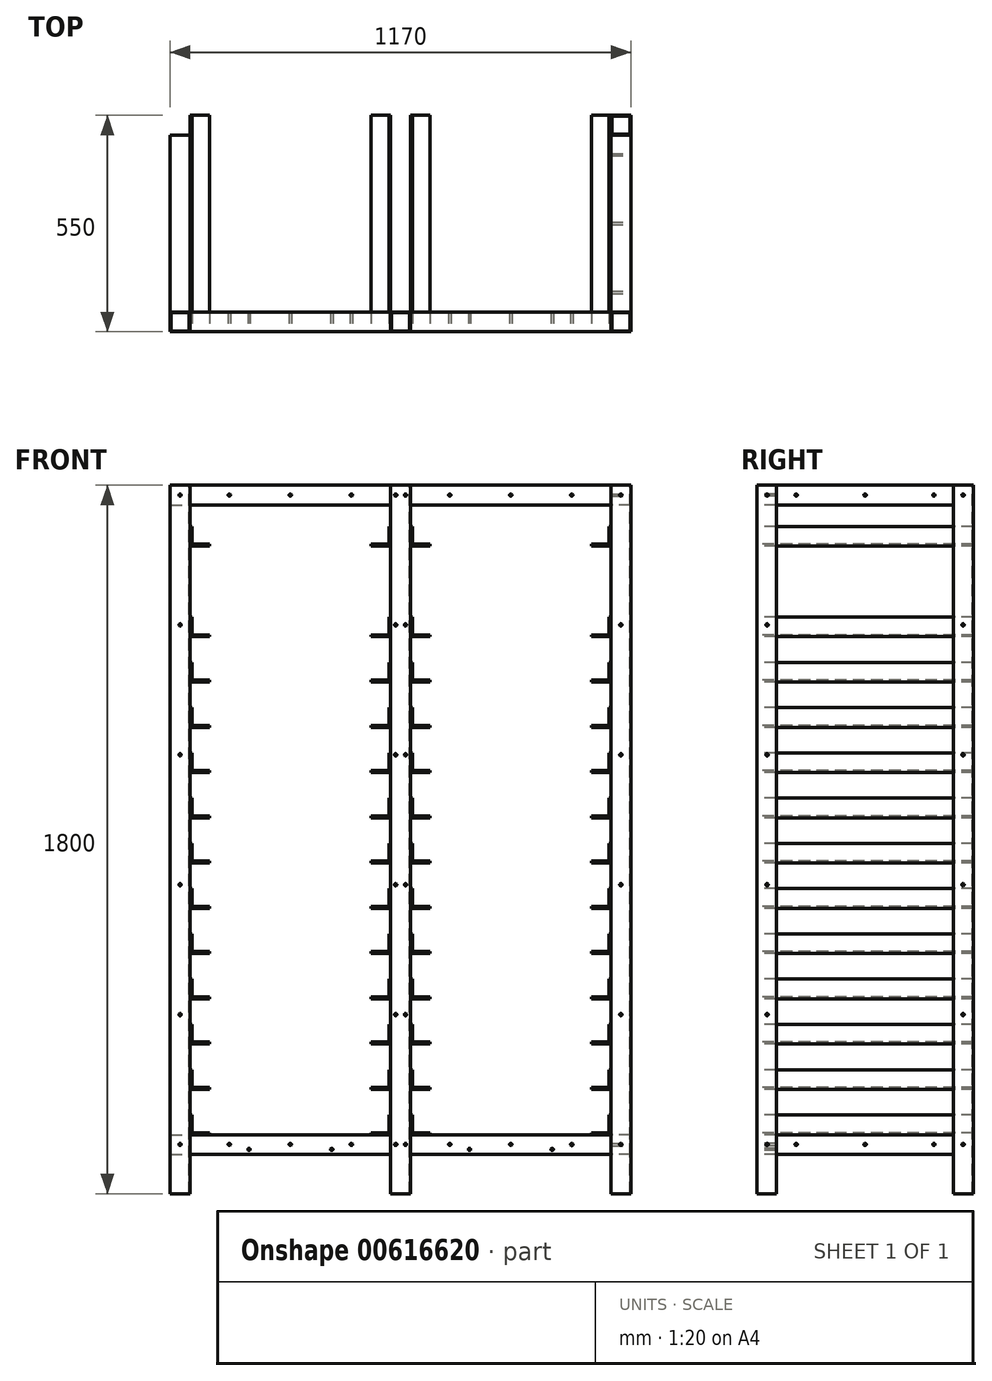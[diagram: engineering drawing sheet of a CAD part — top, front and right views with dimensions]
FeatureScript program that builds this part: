
annotation { "Feature Type Name" : "Feature", "Feature Type Description" : "" }
export const myFeature = defineFeature(function(context is Context, id is Id, definition is map)
    precondition{}
    {
        {
            var Q0;
            Q0=qCreatedBy(makeId("Front.planeOp"),FACE);
            var sketch = newSketch(context, id + "F0", { "sketchPlane" : qUnion([Q0])});
            skLineSegment(sketch, "E0.bottom", {"start": v(-1040.9, 69.44) * mm, "end": v(-990.9, 69.44) * mm});
            skLineSegment(sketch, "E0.top", {"start": v(-1040.9, 1869.44) * mm, "end": v(-990.9, 1869.44) * mm});
            skLineSegment(sketch, "E0.left", {"start": v(-1040.9, 69.44) * mm, "end": v(-1040.9, 1869.44) * mm});
            skLineSegment(sketch, "E0.right", {"start": v(-990.9, 69.44) * mm, "end": v(-990.9, 1869.44) * mm});
            skLineSegment(sketch, "E1.bottom", {"start": v(-990.9, 219.44) * mm, "end": v(-480.9, 219.44) * mm});
            skLineSegment(sketch, "E1.top", {"start": v(-990.9, 169.44) * mm, "end": v(-480.9, 169.44) * mm});
            skLineSegment(sketch, "E1.left", {"start": v(-990.9, 219.44) * mm, "end": v(-990.9, 169.44) * mm});
            skLineSegment(sketch, "E1.right", {"start": v(-480.9, 219.44) * mm, "end": v(-480.9, 169.44) * mm});
            skLineSegment(sketch, "E2.bottom", {"start": v(-980.9, 320.94) * mm, "end": v(-490.9, 320.94) * mm});
            skLineSegment(sketch, "E2.top", {"start": v(-980.9, 224.94) * mm, "end": v(-490.9, 224.94) * mm});
            skLineSegment(sketch, "E2.left", {"start": v(-980.9, 320.94) * mm, "end": v(-980.9, 224.94) * mm});
            skLineSegment(sketch, "E2.right", {"start": v(-490.9, 320.94) * mm, "end": v(-490.9, 224.94) * mm});
            skPoint(sketch, "E3", {"position": v(-990.9, 194.44) * mm});
            skLineSegment(sketch, "E4", {"start": v(-985.9, 269.44) * mm, "end": v(-985.9, 224.44) * mm});
            skLineSegment(sketch, "E5", {"start": v(-985.9, 224.44) * mm, "end": v(-940.9, 224.44) * mm});
            skLineSegment(sketch, "E6", {"start": v(-985.9, 269.44) * mm, "end": v(-990.9, 269.44) * mm});
            skLineSegment(sketch, "E7", {"start": v(-990.9, 269.44) * mm, "end": v(-990.9, 219.44) * mm});
            skLineSegment(sketch, "E8", {"start": v(-990.9, 219.44) * mm, "end": v(-940.9, 219.44) * mm});
            skLineSegment(sketch, "E9", {"start": v(-940.9, 219.44) * mm, "end": v(-940.9, 224.44) * mm});
            skLineSegment(sketch, "E10.0.1.0", {"start": v(-990.9, 384.44) * mm, "end": v(-990.9, 334.44) * mm});
            skLineSegment(sketch, "E10.0.1.1", {"start": v(-985.9, 339.44) * mm, "end": v(-940.9, 339.44) * mm});
            skLineSegment(sketch, "E10.0.1.2", {"start": v(-990.9, 334.44) * mm, "end": v(-940.9, 334.44) * mm});
            skLineSegment(sketch, "E10.0.1.3", {"start": v(-985.9, 384.44) * mm, "end": v(-985.9, 339.44) * mm});
            skLineSegment(sketch, "E10.0.1.4", {"start": v(-940.9, 334.44) * mm, "end": v(-940.9, 339.44) * mm});
            skLineSegment(sketch, "E10.0.1.5", {"start": v(-985.9, 384.44) * mm, "end": v(-990.9, 384.44) * mm});
            skLineSegment(sketch, "E10.0.2.0", {"start": v(-990.9, 499.44) * mm, "end": v(-990.9, 449.44) * mm});
            skLineSegment(sketch, "E10.0.2.1", {"start": v(-985.9, 454.44) * mm, "end": v(-940.9, 454.44) * mm});
            skLineSegment(sketch, "E10.0.2.2", {"start": v(-990.9, 449.44) * mm, "end": v(-940.9, 449.44) * mm});
            skLineSegment(sketch, "E10.0.2.3", {"start": v(-985.9, 499.44) * mm, "end": v(-985.9, 454.44) * mm});
            skLineSegment(sketch, "E10.0.2.4", {"start": v(-940.9, 449.44) * mm, "end": v(-940.9, 454.44) * mm});
            skLineSegment(sketch, "E10.0.2.5", {"start": v(-985.9, 499.44) * mm, "end": v(-990.9, 499.44) * mm});
            skLineSegment(sketch, "E10.0.3.0", {"start": v(-990.9, 614.44) * mm, "end": v(-990.9, 564.44) * mm});
            skLineSegment(sketch, "E10.0.3.1", {"start": v(-985.9, 569.44) * mm, "end": v(-940.9, 569.44) * mm});
            skLineSegment(sketch, "E10.0.3.2", {"start": v(-990.9, 564.44) * mm, "end": v(-940.9, 564.44) * mm});
            skLineSegment(sketch, "E10.0.3.3", {"start": v(-985.9, 614.44) * mm, "end": v(-985.9, 569.44) * mm});
            skLineSegment(sketch, "E10.0.3.4", {"start": v(-940.9, 564.44) * mm, "end": v(-940.9, 569.44) * mm});
            skLineSegment(sketch, "E10.0.3.5", {"start": v(-985.9, 614.44) * mm, "end": v(-990.9, 614.44) * mm});
            skLineSegment(sketch, "E10.0.4.0", {"start": v(-990.9, 729.44) * mm, "end": v(-990.9, 679.44) * mm});
            skLineSegment(sketch, "E10.0.4.1", {"start": v(-985.9, 684.44) * mm, "end": v(-940.9, 684.44) * mm});
            skLineSegment(sketch, "E10.0.4.2", {"start": v(-990.9, 679.44) * mm, "end": v(-940.9, 679.44) * mm});
            skLineSegment(sketch, "E10.0.4.3", {"start": v(-985.9, 729.44) * mm, "end": v(-985.9, 684.44) * mm});
            skLineSegment(sketch, "E10.0.4.4", {"start": v(-940.9, 679.44) * mm, "end": v(-940.9, 684.44) * mm});
            skLineSegment(sketch, "E10.0.4.5", {"start": v(-985.9, 729.44) * mm, "end": v(-990.9, 729.44) * mm});
            skLineSegment(sketch, "E10.0.5.0", {"start": v(-990.9, 844.44) * mm, "end": v(-990.9, 794.44) * mm});
            skLineSegment(sketch, "E10.0.5.1", {"start": v(-985.9, 799.44) * mm, "end": v(-940.9, 799.44) * mm});
            skLineSegment(sketch, "E10.0.5.2", {"start": v(-990.9, 794.44) * mm, "end": v(-940.9, 794.44) * mm});
            skLineSegment(sketch, "E10.0.5.3", {"start": v(-985.9, 844.44) * mm, "end": v(-985.9, 799.44) * mm});
            skLineSegment(sketch, "E10.0.5.4", {"start": v(-940.9, 794.44) * mm, "end": v(-940.9, 799.44) * mm});
            skLineSegment(sketch, "E10.0.5.5", {"start": v(-985.9, 844.44) * mm, "end": v(-990.9, 844.44) * mm});
            skLineSegment(sketch, "E10.0.6.0", {"start": v(-990.9, 959.44) * mm, "end": v(-990.9, 909.44) * mm});
            skLineSegment(sketch, "E10.0.6.1", {"start": v(-985.9, 914.44) * mm, "end": v(-940.9, 914.44) * mm});
            skLineSegment(sketch, "E10.0.6.2", {"start": v(-990.9, 909.44) * mm, "end": v(-940.9, 909.44) * mm});
            skLineSegment(sketch, "E10.0.6.3", {"start": v(-985.9, 959.44) * mm, "end": v(-985.9, 914.44) * mm});
            skLineSegment(sketch, "E10.0.6.4", {"start": v(-940.9, 909.44) * mm, "end": v(-940.9, 914.44) * mm});
            skLineSegment(sketch, "E10.0.6.5", {"start": v(-985.9, 959.44) * mm, "end": v(-990.9, 959.44) * mm});
            skLineSegment(sketch, "E10.0.7.0", {"start": v(-990.9, 1074.44) * mm, "end": v(-990.9, 1024.44) * mm});
            skLineSegment(sketch, "E10.0.7.1", {"start": v(-985.9, 1029.44) * mm, "end": v(-940.9, 1029.44) * mm});
            skLineSegment(sketch, "E10.0.7.2", {"start": v(-990.9, 1024.44) * mm, "end": v(-940.9, 1024.44) * mm});
            skLineSegment(sketch, "E10.0.7.3", {"start": v(-985.9, 1074.44) * mm, "end": v(-985.9, 1029.44) * mm});
            skLineSegment(sketch, "E10.0.7.4", {"start": v(-940.9, 1024.44) * mm, "end": v(-940.9, 1029.44) * mm});
            skLineSegment(sketch, "E10.0.7.5", {"start": v(-985.9, 1074.44) * mm, "end": v(-990.9, 1074.44) * mm});
            skLineSegment(sketch, "E10.0.8.0", {"start": v(-990.9, 1189.44) * mm, "end": v(-990.9, 1139.44) * mm});
            skLineSegment(sketch, "E10.0.8.1", {"start": v(-985.9, 1144.44) * mm, "end": v(-940.9, 1144.44) * mm});
            skLineSegment(sketch, "E10.0.8.2", {"start": v(-990.9, 1139.44) * mm, "end": v(-940.9, 1139.44) * mm});
            skLineSegment(sketch, "E10.0.8.3", {"start": v(-985.9, 1189.44) * mm, "end": v(-985.9, 1144.44) * mm});
            skLineSegment(sketch, "E10.0.8.4", {"start": v(-940.9, 1139.44) * mm, "end": v(-940.9, 1144.44) * mm});
            skLineSegment(sketch, "E10.0.8.5", {"start": v(-985.9, 1189.44) * mm, "end": v(-990.9, 1189.44) * mm});
            skLineSegment(sketch, "E10.0.9.0", {"start": v(-990.9, 1304.44) * mm, "end": v(-990.9, 1254.44) * mm});
            skLineSegment(sketch, "E10.0.9.1", {"start": v(-985.9, 1259.44) * mm, "end": v(-940.9, 1259.44) * mm});
            skLineSegment(sketch, "E10.0.9.2", {"start": v(-990.9, 1254.44) * mm, "end": v(-940.9, 1254.44) * mm});
            skLineSegment(sketch, "E10.0.9.3", {"start": v(-985.9, 1304.44) * mm, "end": v(-985.9, 1259.44) * mm});
            skLineSegment(sketch, "E10.0.9.4", {"start": v(-940.9, 1254.44) * mm, "end": v(-940.9, 1259.44) * mm});
            skLineSegment(sketch, "E10.0.9.5", {"start": v(-985.9, 1304.44) * mm, "end": v(-990.9, 1304.44) * mm});
            skLineSegment(sketch, "E10.0.10.0", {"start": v(-990.9, 1419.44) * mm, "end": v(-990.9, 1369.44) * mm});
            skLineSegment(sketch, "E10.0.10.1", {"start": v(-985.9, 1374.44) * mm, "end": v(-940.9, 1374.44) * mm});
            skLineSegment(sketch, "E10.0.10.2", {"start": v(-990.9, 1369.44) * mm, "end": v(-940.9, 1369.44) * mm});
            skLineSegment(sketch, "E10.0.10.3", {"start": v(-985.9, 1419.44) * mm, "end": v(-985.9, 1374.44) * mm});
            skLineSegment(sketch, "E10.0.10.4", {"start": v(-940.9, 1369.44) * mm, "end": v(-940.9, 1374.44) * mm});
            skLineSegment(sketch, "E10.0.10.5", {"start": v(-985.9, 1419.44) * mm, "end": v(-990.9, 1419.44) * mm});
            skLineSegment(sketch, "E10.0.11.0", {"start": v(-990.9, 1534.44) * mm, "end": v(-990.9, 1484.44) * mm});
            skLineSegment(sketch, "E10.0.11.1", {"start": v(-985.9, 1489.44) * mm, "end": v(-940.9, 1489.44) * mm});
            skLineSegment(sketch, "E10.0.11.2", {"start": v(-990.9, 1484.44) * mm, "end": v(-940.9, 1484.44) * mm});
            skLineSegment(sketch, "E10.0.11.3", {"start": v(-985.9, 1534.44) * mm, "end": v(-985.9, 1489.44) * mm});
            skLineSegment(sketch, "E10.0.11.4", {"start": v(-940.9, 1484.44) * mm, "end": v(-940.9, 1489.44) * mm});
            skLineSegment(sketch, "E10.0.11.5", {"start": v(-985.9, 1534.44) * mm, "end": v(-990.9, 1534.44) * mm});
            skLineSegment(sketch, "E10.direction1", {"start": v(-990.9, 219.44) * mm, "end": v(-950, 219.44) * mm, "construction": true});
            skLineSegment(sketch, "E10.direction2", {"start": v(-990.9, 219.44) * mm, "end": v(-990.9, 334.44) * mm, "construction": true});
            skLineSegment(sketch, "E11", {"start": v(-735.9, 219.44) * mm, "end": v(-735.9, 1014.16) * mm, "construction": true});
            skLineSegment(sketch, "E12.MirrorCS", {"start": v(-530.9, 909.44) * mm, "end": v(-530.9, 914.44) * mm});
            skLineSegment(sketch, "E13.MirrorCS", {"start": v(-485.9, 1074.44) * mm, "end": v(-480.9, 1074.44) * mm});
            skLineSegment(sketch, "E14.MirrorCS", {"start": v(-530.9, 1024.44) * mm, "end": v(-530.9, 1029.44) * mm});
            skLineSegment(sketch, "E15.MirrorCS", {"start": v(-485.9, 1029.44) * mm, "end": v(-530.9, 1029.44) * mm});
            skLineSegment(sketch, "E16.MirrorCS", {"start": v(-485.9, 914.44) * mm, "end": v(-530.9, 914.44) * mm});
            skLineSegment(sketch, "E17.MirrorCS", {"start": v(-485.9, 1304.44) * mm, "end": v(-480.9, 1304.44) * mm});
            skLineSegment(sketch, "E18.MirrorCS", {"start": v(-480.9, 1074.44) * mm, "end": v(-480.9, 1024.44) * mm});
            skLineSegment(sketch, "E19.MirrorCS", {"start": v(-485.9, 1489.44) * mm, "end": v(-530.9, 1489.44) * mm});
            skLineSegment(sketch, "E20.MirrorCS", {"start": v(-485.9, 959.44) * mm, "end": v(-480.9, 959.44) * mm});
            skLineSegment(sketch, "E21.MirrorCS", {"start": v(-485.9, 1304.44) * mm, "end": v(-485.9, 1259.44) * mm});
            skLineSegment(sketch, "E22.MirrorCS", {"start": v(-530.9, 1369.44) * mm, "end": v(-530.9, 1374.44) * mm});
            skLineSegment(sketch, "E23.MirrorCS", {"start": v(-480.9, 1189.44) * mm, "end": v(-480.9, 1139.44) * mm});
            skLineSegment(sketch, "E24.MirrorCS", {"start": v(-485.9, 1144.44) * mm, "end": v(-530.9, 1144.44) * mm});
            skLineSegment(sketch, "E25.MirrorCS", {"start": v(-485.9, 1419.44) * mm, "end": v(-485.9, 1374.44) * mm});
            skLineSegment(sketch, "E26.MirrorCS", {"start": v(-485.9, 959.44) * mm, "end": v(-485.9, 914.44) * mm});
            skLineSegment(sketch, "E27.MirrorCS", {"start": v(-485.9, 1259.44) * mm, "end": v(-530.9, 1259.44) * mm});
            skLineSegment(sketch, "E28.MirrorCS", {"start": v(-485.9, 1534.44) * mm, "end": v(-480.9, 1534.44) * mm});
            skLineSegment(sketch, "E29.MirrorCS", {"start": v(-480.9, 1369.44) * mm, "end": v(-530.9, 1369.44) * mm});
            skLineSegment(sketch, "E30.MirrorCS", {"start": v(-480.9, 1024.44) * mm, "end": v(-530.9, 1024.44) * mm});
            skLineSegment(sketch, "E31.MirrorCS", {"start": v(-480.9, 1419.44) * mm, "end": v(-480.9, 1369.44) * mm});
            skLineSegment(sketch, "E32.MirrorCS", {"start": v(-530.9, 1139.44) * mm, "end": v(-530.9, 1144.44) * mm});
            skLineSegment(sketch, "E33.MirrorCS", {"start": v(-485.9, 1074.44) * mm, "end": v(-485.9, 1029.44) * mm});
            skLineSegment(sketch, "E34.MirrorCS", {"start": v(-480.9, 959.44) * mm, "end": v(-480.9, 909.44) * mm});
            skLineSegment(sketch, "E35.MirrorCS", {"start": v(-485.9, 1189.44) * mm, "end": v(-480.9, 1189.44) * mm});
            skLineSegment(sketch, "E36.MirrorCS", {"start": v(-530.9, 1484.44) * mm, "end": v(-530.9, 1489.44) * mm});
            skLineSegment(sketch, "E37.MirrorCS", {"start": v(-485.9, 1534.44) * mm, "end": v(-485.9, 1489.44) * mm});
            skLineSegment(sketch, "E38.MirrorCS", {"start": v(-480.9, 1484.44) * mm, "end": v(-530.9, 1484.44) * mm});
            skLineSegment(sketch, "E39.MirrorCS", {"start": v(-485.9, 1374.44) * mm, "end": v(-530.9, 1374.44) * mm});
            skLineSegment(sketch, "E40.MirrorCS", {"start": v(-485.9, 269.44) * mm, "end": v(-480.9, 269.44) * mm});
            skLineSegment(sketch, "E41.MirrorCS", {"start": v(-530.9, 1254.44) * mm, "end": v(-530.9, 1259.44) * mm});
            skLineSegment(sketch, "E42.MirrorCS", {"start": v(-485.9, 1189.44) * mm, "end": v(-485.9, 1144.44) * mm});
            skLineSegment(sketch, "E43.MirrorCS", {"start": v(-530.9, 334.44) * mm, "end": v(-530.9, 339.44) * mm});
            skLineSegment(sketch, "E44.MirrorCS", {"start": v(-530.9, 564.44) * mm, "end": v(-530.9, 569.44) * mm});
            skLineSegment(sketch, "E45.MirrorCS", {"start": v(-530.9, 794.44) * mm, "end": v(-530.9, 799.44) * mm});
            skLineSegment(sketch, "E46.MirrorCS", {"start": v(-480.9, 1139.44) * mm, "end": v(-530.9, 1139.44) * mm});
            skLineSegment(sketch, "E47.MirrorCS", {"start": v(-480.9, 1534.44) * mm, "end": v(-480.9, 1484.44) * mm});
            skLineSegment(sketch, "E48.MirrorCS", {"start": v(-480.9, 1254.44) * mm, "end": v(-530.9, 1254.44) * mm});
            skLineSegment(sketch, "E49.MirrorCS", {"start": v(-485.9, 1419.44) * mm, "end": v(-480.9, 1419.44) * mm});
            skLineSegment(sketch, "E50.MirrorCS", {"start": v(-480.9, 334.44) * mm, "end": v(-530.9, 334.44) * mm});
            skLineSegment(sketch, "E51.MirrorCS", {"start": v(-485.9, 799.44) * mm, "end": v(-530.9, 799.44) * mm});
            skLineSegment(sketch, "E52.MirrorCS", {"start": v(-485.9, 339.44) * mm, "end": v(-530.9, 339.44) * mm});
            skLineSegment(sketch, "E53.MirrorCS", {"start": v(-480.9, 1304.44) * mm, "end": v(-480.9, 1254.44) * mm});
            skLineSegment(sketch, "E54.MirrorCS", {"start": v(-480.9, 909.44) * mm, "end": v(-530.9, 909.44) * mm});
            skLineSegment(sketch, "E55.MirrorCS", {"start": v(-480.9, 219.44) * mm, "end": v(-530.9, 219.44) * mm});
            skLineSegment(sketch, "E56.MirrorCS", {"start": v(-485.9, 729.44) * mm, "end": v(-485.9, 684.44) * mm});
            skLineSegment(sketch, "E57.MirrorCS", {"start": v(-480.9, 564.44) * mm, "end": v(-530.9, 564.44) * mm});
            skLineSegment(sketch, "E58.MirrorCS", {"start": v(-480.9, 269.44) * mm, "end": v(-480.9, 219.44) * mm});
            skLineSegment(sketch, "E59.MirrorCS", {"start": v(-485.9, 224.44) * mm, "end": v(-530.9, 224.44) * mm});
            skLineSegment(sketch, "E60.MirrorCS", {"start": v(-480.9, 679.44) * mm, "end": v(-530.9, 679.44) * mm});
            skLineSegment(sketch, "E61.MirrorCS", {"start": v(-485.9, 569.44) * mm, "end": v(-530.9, 569.44) * mm});
            skLineSegment(sketch, "E62.MirrorCS", {"start": v(-485.9, 684.44) * mm, "end": v(-530.9, 684.44) * mm});
            skLineSegment(sketch, "E63.MirrorCS", {"start": v(-530.9, 449.44) * mm, "end": v(-530.9, 454.44) * mm});
            skLineSegment(sketch, "E64.MirrorCS", {"start": v(-480.9, 794.44) * mm, "end": v(-530.9, 794.44) * mm});
            skLineSegment(sketch, "E65.MirrorCS", {"start": v(-480.9, 729.44) * mm, "end": v(-480.9, 679.44) * mm});
            skLineSegment(sketch, "E66.MirrorCS", {"start": v(-485.9, 499.44) * mm, "end": v(-480.9, 499.44) * mm});
            skLineSegment(sketch, "E67.MirrorCS", {"start": v(-485.9, 729.44) * mm, "end": v(-480.9, 729.44) * mm});
            skLineSegment(sketch, "E68.MirrorCS", {"start": v(-485.9, 614.44) * mm, "end": v(-485.9, 569.44) * mm});
            skLineSegment(sketch, "E69.MirrorCS", {"start": v(-480.9, 499.44) * mm, "end": v(-480.9, 449.44) * mm});
            skLineSegment(sketch, "E70.MirrorCS", {"start": v(-530.9, 679.44) * mm, "end": v(-530.9, 684.44) * mm});
            skLineSegment(sketch, "E71.MirrorCS", {"start": v(-485.9, 454.44) * mm, "end": v(-530.9, 454.44) * mm});
            skLineSegment(sketch, "E72.MirrorCS", {"start": v(-480.9, 384.44) * mm, "end": v(-480.9, 334.44) * mm});
            skLineSegment(sketch, "E73.MirrorCS", {"start": v(-530.9, 219.44) * mm, "end": v(-530.9, 224.44) * mm});
            skLineSegment(sketch, "E74.MirrorCS", {"start": v(-485.9, 384.44) * mm, "end": v(-480.9, 384.44) * mm});
            skLineSegment(sketch, "E75.MirrorCS", {"start": v(-485.9, 269.44) * mm, "end": v(-485.9, 224.44) * mm});
            skLineSegment(sketch, "E76.MirrorCS", {"start": v(-485.9, 844.44) * mm, "end": v(-480.9, 844.44) * mm});
            skLineSegment(sketch, "E77.MirrorCS", {"start": v(-480.9, 614.44) * mm, "end": v(-480.9, 564.44) * mm});
            skLineSegment(sketch, "E78.MirrorCS", {"start": v(-480.9, 219.44) * mm, "end": v(-521.8, 219.44) * mm, "construction": true});
            skLineSegment(sketch, "E79.MirrorCS", {"start": v(-480.9, 219.44) * mm, "end": v(-480.9, 334.44) * mm, "construction": true});
            skLineSegment(sketch, "E80.MirrorCS", {"start": v(-485.9, 384.44) * mm, "end": v(-485.9, 339.44) * mm});
            skLineSegment(sketch, "E81.MirrorCS", {"start": v(-485.9, 844.44) * mm, "end": v(-485.9, 799.44) * mm});
            skLineSegment(sketch, "E82.MirrorCS", {"start": v(-485.9, 499.44) * mm, "end": v(-485.9, 454.44) * mm});
            skLineSegment(sketch, "E83.MirrorCS", {"start": v(-485.9, 614.44) * mm, "end": v(-480.9, 614.44) * mm});
            skLineSegment(sketch, "E84.MirrorCS", {"start": v(-480.9, 449.44) * mm, "end": v(-530.9, 449.44) * mm});
            skLineSegment(sketch, "E85.MirrorCS", {"start": v(-480.9, 844.44) * mm, "end": v(-480.9, 794.44) * mm});
            skPoint(sketch, "E86", {"position": v(-735.9, 219.44) * mm});
            skLineSegment(sketch, "E87.0.1.0", {"start": v(-980.9, 435.94) * mm, "end": v(-490.9, 435.94) * mm});
            skLineSegment(sketch, "E87.0.1.1", {"start": v(-980.9, 435.94) * mm, "end": v(-980.9, 339.94) * mm});
            skLineSegment(sketch, "E87.0.1.2", {"start": v(-980.9, 339.94) * mm, "end": v(-490.9, 339.94) * mm});
            skLineSegment(sketch, "E87.0.1.3", {"start": v(-490.9, 435.94) * mm, "end": v(-490.9, 339.94) * mm});
            skLineSegment(sketch, "E87.0.2.0", {"start": v(-980.9, 550.94) * mm, "end": v(-490.9, 550.94) * mm});
            skLineSegment(sketch, "E87.0.2.1", {"start": v(-980.9, 550.94) * mm, "end": v(-980.9, 454.94) * mm});
            skLineSegment(sketch, "E87.0.2.2", {"start": v(-980.9, 454.94) * mm, "end": v(-490.9, 454.94) * mm});
            skLineSegment(sketch, "E87.0.2.3", {"start": v(-490.9, 550.94) * mm, "end": v(-490.9, 454.94) * mm});
            skLineSegment(sketch, "E87.0.3.0", {"start": v(-980.9, 665.94) * mm, "end": v(-490.9, 665.94) * mm});
            skLineSegment(sketch, "E87.0.3.1", {"start": v(-980.9, 665.94) * mm, "end": v(-980.9, 569.94) * mm});
            skLineSegment(sketch, "E87.0.3.2", {"start": v(-980.9, 569.94) * mm, "end": v(-490.9, 569.94) * mm});
            skLineSegment(sketch, "E87.0.3.3", {"start": v(-490.9, 665.94) * mm, "end": v(-490.9, 569.94) * mm});
            skLineSegment(sketch, "E87.0.4.0", {"start": v(-980.9, 780.94) * mm, "end": v(-490.9, 780.94) * mm});
            skLineSegment(sketch, "E87.0.4.1", {"start": v(-980.9, 780.94) * mm, "end": v(-980.9, 684.94) * mm});
            skLineSegment(sketch, "E87.0.4.2", {"start": v(-980.9, 684.94) * mm, "end": v(-490.9, 684.94) * mm});
            skLineSegment(sketch, "E87.0.4.3", {"start": v(-490.9, 780.94) * mm, "end": v(-490.9, 684.94) * mm});
            skLineSegment(sketch, "E87.0.5.0", {"start": v(-980.9, 895.94) * mm, "end": v(-490.9, 895.94) * mm});
            skLineSegment(sketch, "E87.0.5.1", {"start": v(-980.9, 895.94) * mm, "end": v(-980.9, 799.94) * mm});
            skLineSegment(sketch, "E87.0.5.2", {"start": v(-980.9, 799.94) * mm, "end": v(-490.9, 799.94) * mm});
            skLineSegment(sketch, "E87.0.5.3", {"start": v(-490.9, 895.94) * mm, "end": v(-490.9, 799.94) * mm});
            skLineSegment(sketch, "E87.0.6.0", {"start": v(-980.9, 1010.94) * mm, "end": v(-490.9, 1010.94) * mm});
            skLineSegment(sketch, "E87.0.6.1", {"start": v(-980.9, 1010.94) * mm, "end": v(-980.9, 914.94) * mm});
            skLineSegment(sketch, "E87.0.6.2", {"start": v(-980.9, 914.94) * mm, "end": v(-490.9, 914.94) * mm});
            skLineSegment(sketch, "E87.0.6.3", {"start": v(-490.9, 1010.94) * mm, "end": v(-490.9, 914.94) * mm});
            skLineSegment(sketch, "E87.0.7.0", {"start": v(-980.9, 1125.94) * mm, "end": v(-490.9, 1125.94) * mm});
            skLineSegment(sketch, "E87.0.7.1", {"start": v(-980.9, 1125.94) * mm, "end": v(-980.9, 1029.94) * mm});
            skLineSegment(sketch, "E87.0.7.2", {"start": v(-980.9, 1029.94) * mm, "end": v(-490.9, 1029.94) * mm});
            skLineSegment(sketch, "E87.0.7.3", {"start": v(-490.9, 1125.94) * mm, "end": v(-490.9, 1029.94) * mm});
            skLineSegment(sketch, "E87.0.8.0", {"start": v(-980.9, 1240.94) * mm, "end": v(-490.9, 1240.94) * mm});
            skLineSegment(sketch, "E87.0.8.1", {"start": v(-980.9, 1240.94) * mm, "end": v(-980.9, 1144.94) * mm});
            skLineSegment(sketch, "E87.0.8.2", {"start": v(-980.9, 1144.94) * mm, "end": v(-490.9, 1144.94) * mm});
            skLineSegment(sketch, "E87.0.8.3", {"start": v(-490.9, 1240.94) * mm, "end": v(-490.9, 1144.94) * mm});
            skLineSegment(sketch, "E87.0.9.0", {"start": v(-980.9, 1355.94) * mm, "end": v(-490.9, 1355.94) * mm});
            skLineSegment(sketch, "E87.0.9.1", {"start": v(-980.9, 1355.94) * mm, "end": v(-980.9, 1259.94) * mm});
            skLineSegment(sketch, "E87.0.9.2", {"start": v(-980.9, 1259.94) * mm, "end": v(-490.9, 1259.94) * mm});
            skLineSegment(sketch, "E87.0.9.3", {"start": v(-490.9, 1355.94) * mm, "end": v(-490.9, 1259.94) * mm});
            skLineSegment(sketch, "E87.0.10.0", {"start": v(-980.9, 1470.94) * mm, "end": v(-490.9, 1470.94) * mm});
            skLineSegment(sketch, "E87.0.10.1", {"start": v(-980.9, 1470.94) * mm, "end": v(-980.9, 1374.94) * mm});
            skLineSegment(sketch, "E87.0.10.2", {"start": v(-980.9, 1374.94) * mm, "end": v(-490.9, 1374.94) * mm});
            skLineSegment(sketch, "E87.0.10.3", {"start": v(-490.9, 1470.94) * mm, "end": v(-490.9, 1374.94) * mm});
            skLineSegment(sketch, "E87.0.11.0", {"start": v(-980.9, 1585.94) * mm, "end": v(-490.9, 1585.94) * mm});
            skLineSegment(sketch, "E87.0.11.1", {"start": v(-980.9, 1585.94) * mm, "end": v(-980.9, 1489.94) * mm});
            skLineSegment(sketch, "E87.0.11.2", {"start": v(-980.9, 1489.94) * mm, "end": v(-490.9, 1489.94) * mm});
            skLineSegment(sketch, "E87.0.11.3", {"start": v(-490.9, 1585.94) * mm, "end": v(-490.9, 1489.94) * mm});
            skLineSegment(sketch, "E87.direction1", {"start": v(-1017.83, 224.94) * mm, "end": v(-980.9, 224.94) * mm, "construction": true});
            skLineSegment(sketch, "E87.direction2", {"start": v(-980.9, 224.94) * mm, "end": v(-980.9, 339.94) * mm, "construction": true});
            skLineSegment(sketch, "E88.bottom", {"start": v(-990.9, 1869.44) * mm, "end": v(-480.9, 1869.44) * mm});
            skLineSegment(sketch, "E88.top", {"start": v(-990.9, 1819.44) * mm, "end": v(-480.9, 1819.44) * mm});
            skLineSegment(sketch, "E88.left", {"start": v(-990.9, 1869.44) * mm, "end": v(-990.9, 1819.44) * mm});
            skLineSegment(sketch, "E88.right", {"start": v(-480.9, 1869.44) * mm, "end": v(-480.9, 1819.44) * mm});
            skPoint(sketch, "E89", {"position": v(-990.9, 1844.44) * mm});
            skLineSegment(sketch, "E90.0.0.13", {"start": v(-990.9, 1764.44) * mm, "end": v(-990.9, 1714.44) * mm});
            skLineSegment(sketch, "E90.3.0.13", {"start": v(-985.9, 1719.44) * mm, "end": v(-940.9, 1719.44) * mm});
            skLineSegment(sketch, "E90.6.0.13", {"start": v(-990.9, 1714.44) * mm, "end": v(-940.9, 1714.44) * mm});
            skLineSegment(sketch, "E90.9.0.13", {"start": v(-985.9, 1764.44) * mm, "end": v(-985.9, 1719.44) * mm});
            skLineSegment(sketch, "E90.12.0.13", {"start": v(-940.9, 1714.44) * mm, "end": v(-940.9, 1719.44) * mm});
            skLineSegment(sketch, "E90.15.0.13", {"start": v(-985.9, 1764.44) * mm, "end": v(-990.9, 1764.44) * mm});
            skLineSegment(sketch, "E91.MirrorCS", {"start": v(-530.9, 1714.44) * mm, "end": v(-530.9, 1719.44) * mm});
            skLineSegment(sketch, "E92.MirrorCS", {"start": v(-485.9, 1764.44) * mm, "end": v(-480.9, 1764.44) * mm});
            skLineSegment(sketch, "E93.MirrorCS", {"start": v(-480.9, 1764.44) * mm, "end": v(-480.9, 1714.44) * mm});
            skLineSegment(sketch, "E94.MirrorCS", {"start": v(-485.9, 1719.44) * mm, "end": v(-530.9, 1719.44) * mm});
            skLineSegment(sketch, "E95.MirrorCS", {"start": v(-480.9, 1714.44) * mm, "end": v(-530.9, 1714.44) * mm});
            skLineSegment(sketch, "E96.MirrorCS", {"start": v(-485.9, 1764.44) * mm, "end": v(-485.9, 1719.44) * mm});
            skLineSegment(sketch, "E97.1.0.0", {"start": v(-420.9, 1470.94) * mm, "end": v(69.1, 1470.94) * mm});
            skLineSegment(sketch, "E97.1.0.1", {"start": v(-420.9, 1125.94) * mm, "end": v(69.1, 1125.94) * mm});
            skLineSegment(sketch, "E97.1.0.2", {"start": v(-420.9, 1240.94) * mm, "end": v(69.1, 1240.94) * mm});
            skLineSegment(sketch, "E97.1.0.3", {"start": v(-420.9, 780.94) * mm, "end": v(69.1, 780.94) * mm});
            skLineSegment(sketch, "E97.1.0.4", {"start": v(-430.9, 1869.44) * mm, "end": v(79.1, 1869.44) * mm});
            skLineSegment(sketch, "E97.1.0.5", {"start": v(-420.9, 1144.94) * mm, "end": v(69.1, 1144.94) * mm});
            skLineSegment(sketch, "E97.1.0.6", {"start": v(-420.9, 684.94) * mm, "end": v(69.1, 684.94) * mm});
            skLineSegment(sketch, "E97.1.0.7", {"start": v(-480.9, 69.44) * mm, "end": v(-480.9, 1869.44) * mm});
            skLineSegment(sketch, "E97.1.0.8", {"start": v(-430.9, 69.44) * mm, "end": v(-430.9, 1869.44) * mm});
            skLineSegment(sketch, "E97.1.0.9", {"start": v(-430.9, 219.44) * mm, "end": v(79.1, 219.44) * mm});
            skLineSegment(sketch, "E97.1.0.10", {"start": v(-430.9, 169.44) * mm, "end": v(79.1, 169.44) * mm});
            skLineSegment(sketch, "E97.1.0.11", {"start": v(-420.9, 320.94) * mm, "end": v(69.1, 320.94) * mm});
            skLineSegment(sketch, "E97.1.0.12", {"start": v(-420.9, 224.94) * mm, "end": v(69.1, 224.94) * mm});
            skLineSegment(sketch, "E97.1.0.13", {"start": v(-430.9, 1819.44) * mm, "end": v(79.1, 1819.44) * mm});
            skLineSegment(sketch, "E97.1.0.14", {"start": v(-420.9, 895.94) * mm, "end": v(69.1, 895.94) * mm});
            skLineSegment(sketch, "E97.1.0.15", {"start": v(-420.9, 1355.94) * mm, "end": v(69.1, 1355.94) * mm});
            skLineSegment(sketch, "E97.1.0.16", {"start": v(-420.9, 435.94) * mm, "end": v(69.1, 435.94) * mm});
            skPoint(sketch, "E97.1.0.17", {"position": v(-430.9, 194.44) * mm});
            skPoint(sketch, "E97.1.0.18", {"position": v(-175.9, 219.44) * mm});
            skLineSegment(sketch, "E97.1.0.19", {"start": v(-420.9, 1259.94) * mm, "end": v(69.1, 1259.94) * mm});
            skLineSegment(sketch, "E97.1.0.20", {"start": v(-420.9, 799.94) * mm, "end": v(69.1, 799.94) * mm});
            skLineSegment(sketch, "E97.1.0.21", {"start": v(-420.9, 339.94) * mm, "end": v(69.1, 339.94) * mm});
            skPoint(sketch, "E97.1.0.22", {"position": v(-430.9, 1844.44) * mm});
            skLineSegment(sketch, "E97.1.0.23", {"start": v(-420.9, 1010.94) * mm, "end": v(69.1, 1010.94) * mm});
            skLineSegment(sketch, "E97.1.0.24", {"start": v(-420.9, 550.94) * mm, "end": v(69.1, 550.94) * mm});
            skLineSegment(sketch, "E97.1.0.25", {"start": v(-175.9, 219.44) * mm, "end": v(-175.9, 1014.16) * mm, "construction": true});
            skLineSegment(sketch, "E97.1.0.26", {"start": v(-420.9, 914.94) * mm, "end": v(69.1, 914.94) * mm});
            skLineSegment(sketch, "E97.1.0.27", {"start": v(-420.9, 454.94) * mm, "end": v(69.1, 454.94) * mm});
            skLineSegment(sketch, "E97.1.0.28", {"start": v(-420.9, 1374.94) * mm, "end": v(69.1, 1374.94) * mm});
            skLineSegment(sketch, "E97.1.0.29", {"start": v(-420.9, 665.94) * mm, "end": v(69.1, 665.94) * mm});
            skLineSegment(sketch, "E97.1.0.30", {"start": v(-420.9, 1585.94) * mm, "end": v(69.1, 1585.94) * mm});
            skLineSegment(sketch, "E97.1.0.31", {"start": v(-420.9, 1029.94) * mm, "end": v(69.1, 1029.94) * mm});
            skLineSegment(sketch, "E97.1.0.32", {"start": v(-420.9, 569.94) * mm, "end": v(69.1, 569.94) * mm});
            skLineSegment(sketch, "E97.1.0.33", {"start": v(-420.9, 1489.94) * mm, "end": v(69.1, 1489.94) * mm});
            skLineSegment(sketch, "E97.1.0.34", {"start": v(-430.9, 69.44) * mm, "end": v(-430.9, 1869.44) * mm});
            skPoint(sketch, "E97.1.0.35", {"position": v(-430.9, 194.44) * mm});
            skPoint(sketch, "E97.1.0.36", {"position": v(-430.9, 1844.44) * mm});
            skLineSegment(sketch, "E97.1.0.37", {"start": v(69.1, 550.94) * mm, "end": v(69.1, 454.94) * mm});
            skLineSegment(sketch, "E97.1.0.38", {"start": v(74.1, 1419.44) * mm, "end": v(79.1, 1419.44) * mm});
            skLineSegment(sketch, "E97.1.0.39", {"start": v(74.1, 1074.44) * mm, "end": v(74.1, 1029.44) * mm});
            skLineSegment(sketch, "E97.1.0.40", {"start": v(69.1, 1125.94) * mm, "end": v(69.1, 1029.94) * mm});
            skLineSegment(sketch, "E97.1.0.41", {"start": v(69.1, 665.94) * mm, "end": v(69.1, 569.94) * mm});
            skLineSegment(sketch, "E97.1.0.42", {"start": v(79.1, 729.44) * mm, "end": v(79.1, 679.44) * mm});
            skLineSegment(sketch, "E97.1.0.43", {"start": v(69.1, 1585.94) * mm, "end": v(69.1, 1489.94) * mm});
            skLineSegment(sketch, "E97.1.0.44", {"start": v(-380.9, 794.44) * mm, "end": v(-380.9, 799.44) * mm});
            skLineSegment(sketch, "E97.1.0.45", {"start": v(74.1, 729.44) * mm, "end": v(79.1, 729.44) * mm});
            skLineSegment(sketch, "E97.1.0.46", {"start": v(74.1, 1764.44) * mm, "end": v(74.1, 1719.44) * mm});
            skLineSegment(sketch, "E97.1.0.47", {"start": v(74.1, 614.44) * mm, "end": v(74.1, 569.44) * mm});
            skLineSegment(sketch, "E97.1.0.48", {"start": v(29.1, 1484.44) * mm, "end": v(29.1, 1489.44) * mm});
            skLineSegment(sketch, "E97.1.0.49", {"start": v(74.1, 959.44) * mm, "end": v(79.1, 959.44) * mm});
            skLineSegment(sketch, "E97.1.0.50", {"start": v(-480.9, 69.44) * mm, "end": v(-430.9, 69.44) * mm});
            skLineSegment(sketch, "E97.1.0.51", {"start": v(-480.9, 1869.44) * mm, "end": v(-430.9, 1869.44) * mm});
            skLineSegment(sketch, "E97.1.0.52", {"start": v(-430.9, 219.44) * mm, "end": v(-430.9, 169.44) * mm});
            skLineSegment(sketch, "E97.1.0.53", {"start": v(79.1, 219.44) * mm, "end": v(79.1, 169.44) * mm});
            skLineSegment(sketch, "E97.1.0.54", {"start": v(79.1, 499.44) * mm, "end": v(79.1, 449.44) * mm});
            skLineSegment(sketch, "E97.1.0.55", {"start": v(74.1, 1304.44) * mm, "end": v(74.1, 1259.44) * mm});
            skLineSegment(sketch, "E97.1.0.56", {"start": v(69.1, 1240.94) * mm, "end": v(69.1, 1144.94) * mm});
            skLineSegment(sketch, "E97.1.0.57", {"start": v(69.1, 780.94) * mm, "end": v(69.1, 684.94) * mm});
            skLineSegment(sketch, "E97.1.0.58", {"start": v(-380.9, 1484.44) * mm, "end": v(-380.9, 1489.44) * mm});
            skLineSegment(sketch, "E97.1.0.59", {"start": v(-430.9, 909.44) * mm, "end": v(-380.9, 909.44) * mm});
            skLineSegment(sketch, "E97.1.0.60", {"start": v(79.1, 1189.44) * mm, "end": v(79.1, 1139.44) * mm});
            skLineSegment(sketch, "E97.1.0.61", {"start": v(79.1, 1869.44) * mm, "end": v(79.1, 1819.44) * mm});
            skLineSegment(sketch, "E97.1.0.62", {"start": v(69.1, 1355.94) * mm, "end": v(69.1, 1259.94) * mm});
            skLineSegment(sketch, "E97.1.0.63", {"start": v(69.1, 435.94) * mm, "end": v(69.1, 339.94) * mm});
            skLineSegment(sketch, "E97.1.0.64", {"start": v(29.1, 909.44) * mm, "end": v(29.1, 914.44) * mm});
            skLineSegment(sketch, "E97.1.0.65", {"start": v(29.1, 794.44) * mm, "end": v(29.1, 799.44) * mm});
            skLineSegment(sketch, "E97.1.0.66", {"start": v(69.1, 1010.94) * mm, "end": v(69.1, 914.94) * mm});
            skLineSegment(sketch, "E97.1.0.67", {"start": v(69.1, 1470.94) * mm, "end": v(69.1, 1374.94) * mm});
            skLineSegment(sketch, "E97.1.0.68", {"start": v(79.1, 1419.44) * mm, "end": v(79.1, 1369.44) * mm});
            skLineSegment(sketch, "E97.1.0.69", {"start": v(-420.9, 1585.94) * mm, "end": v(-420.9, 1489.94) * mm});
            skLineSegment(sketch, "E97.1.0.70", {"start": v(74.1, 384.44) * mm, "end": v(74.1, 339.44) * mm});
            skLineSegment(sketch, "E97.1.0.71", {"start": v(79.1, 1764.44) * mm, "end": v(79.1, 1714.44) * mm});
            skLineSegment(sketch, "E97.1.0.72", {"start": v(74.1, 384.44) * mm, "end": v(79.1, 384.44) * mm});
            skLineSegment(sketch, "E97.1.0.73", {"start": v(79.1, 219.44) * mm, "end": v(79.1, 334.44) * mm, "construction": true});
            skLineSegment(sketch, "E97.1.0.74", {"start": v(74.1, 1764.44) * mm, "end": v(79.1, 1764.44) * mm});
            skLineSegment(sketch, "E97.1.0.75", {"start": v(79.1, 1074.44) * mm, "end": v(79.1, 1024.44) * mm});
            skLineSegment(sketch, "E97.1.0.76", {"start": v(74.1, 499.44) * mm, "end": v(74.1, 454.44) * mm});
            skLineSegment(sketch, "E97.1.0.77", {"start": v(79.1, 1714.44) * mm, "end": v(29.1, 1714.44) * mm});
            skLineSegment(sketch, "E97.1.0.78", {"start": v(-430.9, 794.44) * mm, "end": v(-380.9, 794.44) * mm});
            skLineSegment(sketch, "E97.1.0.79", {"start": v(74.1, 1719.44) * mm, "end": v(29.1, 1719.44) * mm});
            skLineSegment(sketch, "E97.1.0.80", {"start": v(74.1, 1189.44) * mm, "end": v(79.1, 1189.44) * mm});
            skLineSegment(sketch, "E97.1.0.81", {"start": v(74.1, 614.44) * mm, "end": v(79.1, 614.44) * mm});
            skLineSegment(sketch, "E97.1.0.82", {"start": v(69.1, 320.94) * mm, "end": v(69.1, 224.94) * mm});
            skLineSegment(sketch, "E97.1.0.83", {"start": v(79.1, 1304.44) * mm, "end": v(79.1, 1254.44) * mm});
            skLineSegment(sketch, "E97.1.0.84", {"start": v(-430.9, 1484.44) * mm, "end": v(-380.9, 1484.44) * mm});
            skLineSegment(sketch, "E97.1.0.85", {"start": v(-380.9, 219.44) * mm, "end": v(-380.9, 224.44) * mm});
            skLineSegment(sketch, "E97.1.0.86", {"start": v(-425.9, 914.44) * mm, "end": v(-380.9, 914.44) * mm});
            skLineSegment(sketch, "E97.1.0.87", {"start": v(74.1, 729.44) * mm, "end": v(74.1, 684.44) * mm});
            skLineSegment(sketch, "E97.1.0.88", {"start": v(29.1, 219.44) * mm, "end": v(29.1, 224.44) * mm});
            skLineSegment(sketch, "E97.1.0.89", {"start": v(74.1, 1419.44) * mm, "end": v(74.1, 1374.44) * mm});
            skLineSegment(sketch, "E97.1.0.90", {"start": v(74.1, 1534.44) * mm, "end": v(79.1, 1534.44) * mm});
            skLineSegment(sketch, "E97.1.0.91", {"start": v(79.1, 269.44) * mm, "end": v(79.1, 219.44) * mm});
            skLineSegment(sketch, "E97.1.0.92", {"start": v(74.1, 1189.44) * mm, "end": v(74.1, 1144.44) * mm});
            skLineSegment(sketch, "E97.1.0.93", {"start": v(-380.9, 334.44) * mm, "end": v(-380.9, 339.44) * mm});
            skLineSegment(sketch, "E97.1.0.94", {"start": v(-380.9, 1254.44) * mm, "end": v(-380.9, 1259.44) * mm});
            skLineSegment(sketch, "E97.1.0.95", {"start": v(74.1, 269.44) * mm, "end": v(74.1, 224.44) * mm});
            skLineSegment(sketch, "E97.1.0.96", {"start": v(74.1, 224.44) * mm, "end": v(29.1, 224.44) * mm});
            skLineSegment(sketch, "E97.1.0.97", {"start": v(74.1, 1259.44) * mm, "end": v(29.1, 1259.44) * mm});
            skLineSegment(sketch, "E97.1.0.98", {"start": v(-420.9, 1470.94) * mm, "end": v(-420.9, 1374.94) * mm});
            skLineSegment(sketch, "E97.1.0.99", {"start": v(-425.9, 1764.44) * mm, "end": v(-425.9, 1719.44) * mm});
            skLineSegment(sketch, "E97.1.0.100", {"start": v(-420.9, 1010.94) * mm, "end": v(-420.9, 914.94) * mm});
            skLineSegment(sketch, "E97.1.0.101", {"start": v(-420.9, 550.94) * mm, "end": v(-420.9, 454.94) * mm});
            skLineSegment(sketch, "E97.1.0.102", {"start": v(-380.9, 679.44) * mm, "end": v(-380.9, 684.44) * mm});
            skLineSegment(sketch, "E97.1.0.103", {"start": v(79.1, 1369.44) * mm, "end": v(29.1, 1369.44) * mm});
            skLineSegment(sketch, "E97.1.0.104", {"start": v(74.1, 1074.44) * mm, "end": v(79.1, 1074.44) * mm});
            skLineSegment(sketch, "E97.1.0.105", {"start": v(-425.9, 1764.44) * mm, "end": v(-430.9, 1764.44) * mm});
            skLineSegment(sketch, "E97.1.0.106", {"start": v(-425.9, 729.44) * mm, "end": v(-430.9, 729.44) * mm});
            skLineSegment(sketch, "E97.1.0.107", {"start": v(79.1, 1139.44) * mm, "end": v(29.1, 1139.44) * mm});
            skLineSegment(sketch, "E97.1.0.108", {"start": v(-380.9, 1024.44) * mm, "end": v(-380.9, 1029.44) * mm});
            skLineSegment(sketch, "E97.1.0.109", {"start": v(79.1, 1534.44) * mm, "end": v(79.1, 1484.44) * mm});
            skLineSegment(sketch, "E97.1.0.110", {"start": v(-420.9, 1125.94) * mm, "end": v(-420.9, 1029.94) * mm});
            skLineSegment(sketch, "E97.1.0.111", {"start": v(-425.9, 1074.44) * mm, "end": v(-430.9, 1074.44) * mm});
            skLineSegment(sketch, "E97.1.0.112", {"start": v(-425.9, 1419.44) * mm, "end": v(-430.9, 1419.44) * mm});
            skLineSegment(sketch, "E97.1.0.113", {"start": v(-425.9, 499.44) * mm, "end": v(-430.9, 499.44) * mm});
            skLineSegment(sketch, "E97.1.0.114", {"start": v(74.1, 499.44) * mm, "end": v(79.1, 499.44) * mm});
            skLineSegment(sketch, "E97.1.0.115", {"start": v(79.1, 334.44) * mm, "end": v(29.1, 334.44) * mm});
            skLineSegment(sketch, "E97.1.0.116", {"start": v(79.1, 959.44) * mm, "end": v(79.1, 909.44) * mm});
            skLineSegment(sketch, "E97.1.0.117", {"start": v(-380.9, 449.44) * mm, "end": v(-380.9, 454.44) * mm});
            skLineSegment(sketch, "E97.1.0.118", {"start": v(74.1, 1304.44) * mm, "end": v(79.1, 1304.44) * mm});
            skLineSegment(sketch, "E97.1.0.119", {"start": v(-380.9, 1369.44) * mm, "end": v(-380.9, 1374.44) * mm});
            skLineSegment(sketch, "E97.1.0.120", {"start": v(74.1, 1489.44) * mm, "end": v(29.1, 1489.44) * mm});
            skLineSegment(sketch, "E97.1.0.121", {"start": v(-420.9, 224.94) * mm, "end": v(-420.9, 339.94) * mm, "construction": true});
            skLineSegment(sketch, "E97.1.0.122", {"start": v(-420.9, 1240.94) * mm, "end": v(-420.9, 1144.94) * mm});
            skLineSegment(sketch, "E97.1.0.123", {"start": v(-420.9, 780.94) * mm, "end": v(-420.9, 684.94) * mm});
            skLineSegment(sketch, "E97.1.0.124", {"start": v(-425.9, 1489.44) * mm, "end": v(-380.9, 1489.44) * mm});
            skLineSegment(sketch, "E97.1.0.125", {"start": v(74.1, 339.44) * mm, "end": v(29.1, 339.44) * mm});
            skLineSegment(sketch, "E97.1.0.126", {"start": v(79.1, 449.44) * mm, "end": v(29.1, 449.44) * mm});
            skLineSegment(sketch, "E97.1.0.127", {"start": v(74.1, 1534.44) * mm, "end": v(74.1, 1489.44) * mm});
            skLineSegment(sketch, "E97.1.0.128", {"start": v(-430.9, 219.44) * mm, "end": v(-380.9, 219.44) * mm});
            skLineSegment(sketch, "E97.1.0.129", {"start": v(-380.9, 1139.44) * mm, "end": v(-380.9, 1144.44) * mm});
            skLineSegment(sketch, "E97.1.0.130", {"start": v(-430.9, 959.44) * mm, "end": v(-430.9, 909.44) * mm});
            skLineSegment(sketch, "E97.1.0.131", {"start": v(-430.9, 1869.44) * mm, "end": v(-430.9, 1819.44) * mm});
            skLineSegment(sketch, "E97.1.0.132", {"start": v(-425.9, 1189.44) * mm, "end": v(-430.9, 1189.44) * mm});
            skLineSegment(sketch, "E97.1.0.133", {"start": v(-425.9, 614.44) * mm, "end": v(-425.9, 569.44) * mm});
            skLineSegment(sketch, "E97.1.0.134", {"start": v(29.1, 679.44) * mm, "end": v(29.1, 684.44) * mm});
            skLineSegment(sketch, "E97.1.0.135", {"start": v(79.1, 909.44) * mm, "end": v(29.1, 909.44) * mm});
            skLineSegment(sketch, "E97.1.0.136", {"start": v(79.1, 1484.44) * mm, "end": v(29.1, 1484.44) * mm});
            skLineSegment(sketch, "E97.1.0.137", {"start": v(-430.9, 384.44) * mm, "end": v(-430.9, 334.44) * mm});
            skLineSegment(sketch, "E97.1.0.138", {"start": v(-430.9, 1304.44) * mm, "end": v(-430.9, 1254.44) * mm});
            skLineSegment(sketch, "E97.1.0.139", {"start": v(-380.9, 564.44) * mm, "end": v(-380.9, 569.44) * mm});
            skLineSegment(sketch, "E97.1.0.140", {"start": v(74.1, 454.44) * mm, "end": v(29.1, 454.44) * mm});
            skLineSegment(sketch, "E97.1.0.141", {"start": v(79.1, 219.44) * mm, "end": v(29.1, 219.44) * mm});
            skLineSegment(sketch, "E97.1.0.142", {"start": v(74.1, 1374.44) * mm, "end": v(29.1, 1374.44) * mm});
            skLineSegment(sketch, "E97.1.0.143", {"start": v(-420.9, 1355.94) * mm, "end": v(-420.9, 1259.94) * mm});
            skLineSegment(sketch, "E97.1.0.144", {"start": v(-420.9, 435.94) * mm, "end": v(-420.9, 339.94) * mm});
            skLineSegment(sketch, "E97.1.0.145", {"start": v(79.1, 384.44) * mm, "end": v(79.1, 334.44) * mm});
            skLineSegment(sketch, "E97.1.0.146", {"start": v(74.1, 269.44) * mm, "end": v(79.1, 269.44) * mm});
            skLineSegment(sketch, "E97.1.0.147", {"start": v(-380.9, 909.44) * mm, "end": v(-380.9, 914.44) * mm});
            skLineSegment(sketch, "E97.1.0.148", {"start": v(69.1, 895.94) * mm, "end": v(69.1, 799.94) * mm});
            skLineSegment(sketch, "E97.1.0.149", {"start": v(74.1, 959.44) * mm, "end": v(74.1, 914.44) * mm});
            skLineSegment(sketch, "E97.1.0.150", {"start": v(-430.9, 1714.44) * mm, "end": v(-380.9, 1714.44) * mm});
            skLineSegment(sketch, "E97.1.0.151", {"start": v(74.1, 844.44) * mm, "end": v(79.1, 844.44) * mm});
            skLineSegment(sketch, "E97.1.0.152", {"start": v(79.1, 679.44) * mm, "end": v(29.1, 679.44) * mm});
            skLineSegment(sketch, "E97.1.0.153", {"start": v(-380.9, 1714.44) * mm, "end": v(-380.9, 1719.44) * mm});
            skLineSegment(sketch, "E97.1.0.154", {"start": v(79.1, 614.44) * mm, "end": v(79.1, 564.44) * mm});
            skLineSegment(sketch, "E97.1.0.155", {"start": v(79.1, 219.44) * mm, "end": v(38.2, 219.44) * mm, "construction": true});
            skLineSegment(sketch, "E97.1.0.156", {"start": v(74.1, 684.44) * mm, "end": v(29.1, 684.44) * mm});
            skLineSegment(sketch, "E97.1.0.157", {"start": v(29.1, 1714.44) * mm, "end": v(29.1, 1719.44) * mm});
            skLineSegment(sketch, "E97.1.0.158", {"start": v(-420.9, 665.94) * mm, "end": v(-420.9, 569.94) * mm});
            skLineSegment(sketch, "E97.1.0.159", {"start": v(-425.9, 799.44) * mm, "end": v(-380.9, 799.44) * mm});
            skLineSegment(sketch, "E97.1.0.160", {"start": v(79.1, 1254.44) * mm, "end": v(29.1, 1254.44) * mm});
            skLineSegment(sketch, "E97.1.0.161", {"start": v(29.1, 1139.44) * mm, "end": v(29.1, 1144.44) * mm});
            skLineSegment(sketch, "E97.1.0.162", {"start": v(74.1, 914.44) * mm, "end": v(29.1, 914.44) * mm});
            skLineSegment(sketch, "E97.1.0.163", {"start": v(-425.9, 1419.44) * mm, "end": v(-425.9, 1374.44) * mm});
            skLineSegment(sketch, "E97.1.0.164", {"start": v(-425.9, 959.44) * mm, "end": v(-430.9, 959.44) * mm});
            skLineSegment(sketch, "E97.1.0.165", {"start": v(-430.9, 679.44) * mm, "end": v(-380.9, 679.44) * mm});
            skLineSegment(sketch, "E97.1.0.166", {"start": v(29.1, 334.44) * mm, "end": v(29.1, 339.44) * mm});
            skLineSegment(sketch, "E97.1.0.167", {"start": v(-430.9, 1024.44) * mm, "end": v(-380.9, 1024.44) * mm});
            skLineSegment(sketch, "E97.1.0.168", {"start": v(74.1, 569.44) * mm, "end": v(29.1, 569.44) * mm});
            skLineSegment(sketch, "E97.1.0.169", {"start": v(-425.9, 1074.44) * mm, "end": v(-425.9, 1029.44) * mm});
            skLineSegment(sketch, "E97.1.0.170", {"start": v(-425.9, 454.44) * mm, "end": v(-380.9, 454.44) * mm});
            skLineSegment(sketch, "E97.1.0.171", {"start": v(79.1, 1024.44) * mm, "end": v(29.1, 1024.44) * mm});
            skLineSegment(sketch, "E97.1.0.172", {"start": v(-430.9, 449.44) * mm, "end": v(-380.9, 449.44) * mm});
            skLineSegment(sketch, "E97.1.0.173", {"start": v(74.1, 1029.44) * mm, "end": v(29.1, 1029.44) * mm});
            skLineSegment(sketch, "E97.1.0.174", {"start": v(-425.9, 1144.44) * mm, "end": v(-380.9, 1144.44) * mm});
            skLineSegment(sketch, "E97.1.0.175", {"start": v(74.1, 844.44) * mm, "end": v(74.1, 799.44) * mm});
            skLineSegment(sketch, "E97.1.0.176", {"start": v(-430.9, 1139.44) * mm, "end": v(-380.9, 1139.44) * mm});
            skLineSegment(sketch, "E97.1.0.177", {"start": v(-430.9, 614.44) * mm, "end": v(-430.9, 564.44) * mm});
            skLineSegment(sketch, "E97.1.0.178", {"start": v(74.1, 799.44) * mm, "end": v(29.1, 799.44) * mm});
            skLineSegment(sketch, "E97.1.0.179", {"start": v(-425.9, 1189.44) * mm, "end": v(-425.9, 1144.44) * mm});
            skLineSegment(sketch, "E97.1.0.180", {"start": v(-425.9, 569.44) * mm, "end": v(-380.9, 569.44) * mm});
            skLineSegment(sketch, "E97.1.0.181", {"start": v(-425.9, 224.44) * mm, "end": v(-380.9, 224.44) * mm});
            skLineSegment(sketch, "E97.1.0.182", {"start": v(79.1, 844.44) * mm, "end": v(79.1, 794.44) * mm});
            skLineSegment(sketch, "E97.1.0.183", {"start": v(-430.9, 564.44) * mm, "end": v(-380.9, 564.44) * mm});
            skLineSegment(sketch, "E97.1.0.184", {"start": v(29.1, 1369.44) * mm, "end": v(29.1, 1374.44) * mm});
            skLineSegment(sketch, "E97.1.0.185", {"start": v(-420.9, 895.94) * mm, "end": v(-420.9, 799.94) * mm});
            skLineSegment(sketch, "E97.1.0.186", {"start": v(-425.9, 1259.44) * mm, "end": v(-380.9, 1259.44) * mm});
            skLineSegment(sketch, "E97.1.0.187", {"start": v(-425.9, 959.44) * mm, "end": v(-425.9, 914.44) * mm});
            skLineSegment(sketch, "E97.1.0.188", {"start": v(74.1, 1144.44) * mm, "end": v(29.1, 1144.44) * mm});
            skLineSegment(sketch, "E97.1.0.189", {"start": v(-430.9, 1764.44) * mm, "end": v(-430.9, 1714.44) * mm});
            skLineSegment(sketch, "E97.1.0.190", {"start": v(-430.9, 334.44) * mm, "end": v(-380.9, 334.44) * mm});
            skLineSegment(sketch, "E97.1.0.191", {"start": v(-430.9, 1254.44) * mm, "end": v(-380.9, 1254.44) * mm});
            skLineSegment(sketch, "E97.1.0.192", {"start": v(79.1, 564.44) * mm, "end": v(29.1, 564.44) * mm});
            skLineSegment(sketch, "E97.1.0.193", {"start": v(29.1, 1254.44) * mm, "end": v(29.1, 1259.44) * mm});
            skLineSegment(sketch, "E97.1.0.194", {"start": v(-425.9, 1719.44) * mm, "end": v(-380.9, 1719.44) * mm});
            skLineSegment(sketch, "E97.1.0.195", {"start": v(-430.9, 219.44) * mm, "end": v(-430.9, 334.44) * mm, "construction": true});
            skLineSegment(sketch, "E97.1.0.196", {"start": v(-425.9, 729.44) * mm, "end": v(-425.9, 684.44) * mm});
            skLineSegment(sketch, "E97.1.0.197", {"start": v(-425.9, 384.44) * mm, "end": v(-430.9, 384.44) * mm});
            skLineSegment(sketch, "E97.1.0.198", {"start": v(29.1, 564.44) * mm, "end": v(29.1, 569.44) * mm});
            skLineSegment(sketch, "E97.1.0.199", {"start": v(-425.9, 1304.44) * mm, "end": v(-430.9, 1304.44) * mm});
            skLineSegment(sketch, "E97.1.0.200", {"start": v(-430.9, 1419.44) * mm, "end": v(-430.9, 1369.44) * mm});
            skLineSegment(sketch, "E97.1.0.201", {"start": v(-430.9, 1369.44) * mm, "end": v(-380.9, 1369.44) * mm});
            skLineSegment(sketch, "E97.1.0.202", {"start": v(29.1, 449.44) * mm, "end": v(29.1, 454.44) * mm});
            skLineSegment(sketch, "E97.1.0.203", {"start": v(-425.9, 499.44) * mm, "end": v(-425.9, 454.44) * mm});
            skLineSegment(sketch, "E97.1.0.204", {"start": v(79.1, 794.44) * mm, "end": v(29.1, 794.44) * mm});
            skLineSegment(sketch, "E97.1.0.205", {"start": v(-425.9, 684.44) * mm, "end": v(-380.9, 684.44) * mm});
            skLineSegment(sketch, "E97.1.0.206", {"start": v(-430.9, 1074.44) * mm, "end": v(-430.9, 1024.44) * mm});
            skLineSegment(sketch, "E97.1.0.207", {"start": v(-425.9, 1374.44) * mm, "end": v(-380.9, 1374.44) * mm});
            skLineSegment(sketch, "E97.1.0.208", {"start": v(29.1, 1024.44) * mm, "end": v(29.1, 1029.44) * mm});
            skLineSegment(sketch, "E97.1.0.209", {"start": v(-430.9, 844.44) * mm, "end": v(-430.9, 794.44) * mm});
            skLineSegment(sketch, "E97.1.0.210", {"start": v(-425.9, 844.44) * mm, "end": v(-425.9, 799.44) * mm});
            skLineSegment(sketch, "E97.1.0.211", {"start": v(-430.9, 1189.44) * mm, "end": v(-430.9, 1139.44) * mm});
            skLineSegment(sketch, "E97.1.0.212", {"start": v(-430.9, 1534.44) * mm, "end": v(-430.9, 1484.44) * mm});
            skLineSegment(sketch, "E97.1.0.213", {"start": v(-425.9, 844.44) * mm, "end": v(-430.9, 844.44) * mm});
            skLineSegment(sketch, "E97.1.0.214", {"start": v(-420.9, 320.94) * mm, "end": v(-420.9, 224.94) * mm});
            skLineSegment(sketch, "E97.1.0.215", {"start": v(-425.9, 269.44) * mm, "end": v(-425.9, 224.44) * mm});
            skLineSegment(sketch, "E97.1.0.216", {"start": v(-425.9, 1534.44) * mm, "end": v(-425.9, 1489.44) * mm});
            skLineSegment(sketch, "E97.1.0.217", {"start": v(-425.9, 339.44) * mm, "end": v(-380.9, 339.44) * mm});
            skLineSegment(sketch, "E97.1.0.218", {"start": v(-425.9, 614.44) * mm, "end": v(-430.9, 614.44) * mm});
            skLineSegment(sketch, "E97.1.0.219", {"start": v(-430.9, 729.44) * mm, "end": v(-430.9, 679.44) * mm});
            skLineSegment(sketch, "E97.1.0.220", {"start": v(-425.9, 384.44) * mm, "end": v(-425.9, 339.44) * mm});
            skLineSegment(sketch, "E97.1.0.221", {"start": v(-425.9, 1304.44) * mm, "end": v(-425.9, 1259.44) * mm});
            skLineSegment(sketch, "E97.1.0.222", {"start": v(-425.9, 1029.44) * mm, "end": v(-380.9, 1029.44) * mm});
            skLineSegment(sketch, "E97.1.0.223", {"start": v(-430.9, 499.44) * mm, "end": v(-430.9, 449.44) * mm});
            skLineSegment(sketch, "E97.1.0.224", {"start": v(-430.9, 269.44) * mm, "end": v(-430.9, 219.44) * mm});
            skLineSegment(sketch, "E97.1.0.225", {"start": v(-425.9, 1534.44) * mm, "end": v(-430.9, 1534.44) * mm});
            skLineSegment(sketch, "E97.1.0.226", {"start": v(-457.83, 224.94) * mm, "end": v(-420.9, 224.94) * mm, "construction": true});
            skLineSegment(sketch, "E97.1.0.227", {"start": v(-425.9, 269.44) * mm, "end": v(-430.9, 269.44) * mm});
            skLineSegment(sketch, "E97.1.0.228", {"start": v(-430.9, 219.44) * mm, "end": v(-390, 219.44) * mm, "construction": true});
            skLineSegment(sketch, "E97.2.0.7", {"start": v(79.1, 69.44) * mm, "end": v(79.1, 1869.44) * mm});
            skLineSegment(sketch, "E97.2.0.50", {"start": v(79.1, 69.44) * mm, "end": v(129.1, 69.44) * mm});
            skLineSegment(sketch, "E97.2.0.51", {"start": v(79.1, 1869.44) * mm, "end": v(129.1, 1869.44) * mm});
            skLineSegment(sketch, "E97.direction1", {"start": v(-1040.9, 69.44) * mm, "end": v(-480.9, 69.44) * mm, "construction": true});
            skLineSegment(sketch, "E98", {"start": v(129.1, 69.44) * mm, "end": v(129.1, 1869.44) * mm});
            skSolve(sketch);
        }
        {
            var Q0;
            Q0=makeQuery(id+"F0.imprint","IMPRINT",FACE,{"disambiguationData":[TD([[makeQuery(id+"F0.imprint","IMPRINT",EDGE,{"derivedFrom":sQuery(id+"F0.wireOp",EDGE,"E90.3.0.13")}),-1.0]])]});
            var Q1;
            Q1=makeQuery(id+"F0.imprint","IMPRINT",FACE,{"disambiguationData":[TD([[makeQuery(id+"F0.imprint","IMPRINT",EDGE,{"derivedFrom":sQuery(id+"F0.wireOp",EDGE,"E91.MirrorCS")}),-1.0]])]});
            var Q2;
            Q2=makeQuery(id+"F0.imprint","IMPRINT",FACE,{"disambiguationData":[TD([[makeQuery(id+"F0.imprint","IMPRINT",EDGE,{"derivedFrom":sQuery(id+"F0.wireOp",EDGE,"E10.0.11.1")}),-1.0]])]});
            var Q3;
            Q3=makeQuery(id+"F0.imprint","IMPRINT",FACE,{"disambiguationData":[TD([[makeQuery(id+"F0.imprint","IMPRINT",EDGE,{"derivedFrom":sQuery(id+"F0.wireOp",EDGE,"E10.0.10.1")}),-1.0]])]});
            var Q4;
            Q4=makeQuery(id+"F0.imprint","IMPRINT",FACE,{"disambiguationData":[TD([[makeQuery(id+"F0.imprint","IMPRINT",EDGE,{"derivedFrom":sQuery(id+"F0.wireOp",EDGE,"E10.0.9.1")}),-1.0]])]});
            var Q5;
            Q5=makeQuery(id+"F0.imprint","IMPRINT",FACE,{"disambiguationData":[TD([[makeQuery(id+"F0.imprint","IMPRINT",EDGE,{"derivedFrom":sQuery(id+"F0.wireOp",EDGE,"E10.0.8.1")}),-1.0]])]});
            var Q6;
            Q6=makeQuery(id+"F0.imprint","IMPRINT",FACE,{"disambiguationData":[TD([[makeQuery(id+"F0.imprint","IMPRINT",EDGE,{"derivedFrom":sQuery(id+"F0.wireOp",EDGE,"E10.0.7.1")}),-1.0]])]});
            var Q7;
            Q7=makeQuery(id+"F0.imprint","IMPRINT",FACE,{"disambiguationData":[TD([[makeQuery(id+"F0.imprint","IMPRINT",EDGE,{"derivedFrom":sQuery(id+"F0.wireOp",EDGE,"E10.0.6.1")}),-1.0]])]});
            var Q8;
            Q8=makeQuery(id+"F0.imprint","IMPRINT",FACE,{"disambiguationData":[TD([[makeQuery(id+"F0.imprint","IMPRINT",EDGE,{"derivedFrom":sQuery(id+"F0.wireOp",EDGE,"E10.0.4.1")}),-1.0]])]});
            var Q9;
            Q9=makeQuery(id+"F0.imprint","IMPRINT",FACE,{"disambiguationData":[TD([[makeQuery(id+"F0.imprint","IMPRINT",EDGE,{"derivedFrom":sQuery(id+"F0.wireOp",EDGE,"E10.0.5.1")}),-1.0]])]});
            var Q10;
            Q10=makeQuery(id+"F0.imprint","IMPRINT",FACE,{"disambiguationData":[TD([[makeQuery(id+"F0.imprint","IMPRINT",EDGE,{"derivedFrom":sQuery(id+"F0.wireOp",EDGE,"E10.0.3.1")}),-1.0]])]});
            var Q11;
            Q11=makeQuery(id+"F0.imprint","IMPRINT",FACE,{"disambiguationData":[TD([[makeQuery(id+"F0.imprint","IMPRINT",EDGE,{"derivedFrom":sQuery(id+"F0.wireOp",EDGE,"E10.0.2.1")}),-1.0]])]});
            var Q12;
            Q12=makeQuery(id+"F0.imprint","IMPRINT",FACE,{"disambiguationData":[TD([[makeQuery(id+"F0.imprint","IMPRINT",EDGE,{"derivedFrom":sQuery(id+"F0.wireOp",EDGE,"E10.0.1.1")}),-1.0]])]});
            var Q13;
            Q13=makeQuery(id+"F0.imprint","IMPRINT",FACE,{"disambiguationData":[TD([[makeQuery(id+"F0.imprint","IMPRINT",EDGE,{"derivedFrom":sQuery(id+"F0.wireOp",EDGE,"E4")}),-1.0]])]});
            var Q14;
            Q14=makeQuery(id+"F0.imprint","IMPRINT",FACE,{"disambiguationData":[TD([[makeQuery(id+"F0.imprint","IMPRINT",EDGE,{"derivedFrom":sQuery(id+"F0.wireOp",EDGE,"E97.1.0.93")}),1.0]])]});
            var Q15;
            Q15=makeQuery(id+"F0.imprint","IMPRINT",FACE,{"disambiguationData":[TD([[makeQuery(id+"F0.imprint","IMPRINT",EDGE,{"derivedFrom":sQuery(id+"F0.wireOp",EDGE,"E97.1.0.85")}),1.0]])]});
            var Q16;
            {var subQ1=sQuery(id+"F0.wireOp",EDGE,"E40.MirrorCS");Q16=makeQuery(id+"F0.imprint","IMPRINT",FACE,{"disambiguationData":[TD([[makeQuery(id+"F0.imprint","IMPRINT",EDGE,{"derivedFrom":subQ1}),-1.0]])]});}
            var Q17;
            Q17=makeQuery(id+"F0.imprint","IMPRINT",FACE,{"disambiguationData":[TD([[makeQuery(id+"F0.imprint","IMPRINT",EDGE,{"derivedFrom":sQuery(id+"F0.wireOp",EDGE,"E43.MirrorCS")}),-1.0]])]});
            var Q18;
            Q18=makeQuery(id+"F0.imprint","IMPRINT",FACE,{"disambiguationData":[TD([[makeQuery(id+"F0.imprint","IMPRINT",EDGE,{"derivedFrom":sQuery(id+"F0.wireOp",EDGE,"E44.MirrorCS")}),-1.0]])]});
            var Q19;
            Q19=makeQuery(id+"F0.imprint","IMPRINT",FACE,{"disambiguationData":[TD([[makeQuery(id+"F0.imprint","IMPRINT",EDGE,{"derivedFrom":sQuery(id+"F0.wireOp",EDGE,"E97.1.0.133")}),-1.0]])]});
            var Q20;
            Q20=makeQuery(id+"F0.imprint","IMPRINT",FACE,{"disambiguationData":[TD([[makeQuery(id+"F0.imprint","IMPRINT",EDGE,{"derivedFrom":sQuery(id+"F0.wireOp",EDGE,"E97.1.0.113")}),1.0]])]});
            var Q21;
            Q21=makeQuery(id+"F0.imprint","IMPRINT",FACE,{"disambiguationData":[TD([[makeQuery(id+"F0.imprint","IMPRINT",EDGE,{"derivedFrom":sQuery(id+"F0.wireOp",EDGE,"E63.MirrorCS")}),-1.0]])]});
            var Q22;
            Q22=makeQuery(id+"F0.imprint","IMPRINT",FACE,{"disambiguationData":[TD([[makeQuery(id+"F0.imprint","IMPRINT",EDGE,{"derivedFrom":sQuery(id+"F0.wireOp",EDGE,"E56.MirrorCS")}),1.0]])]});
            var Q23;
            Q23=makeQuery(id+"F0.imprint","IMPRINT",FACE,{"disambiguationData":[TD([[makeQuery(id+"F0.imprint","IMPRINT",EDGE,{"derivedFrom":sQuery(id+"F0.wireOp",EDGE,"E97.1.0.102")}),1.0]])]});
            var Q24;
            Q24=makeQuery(id+"F0.imprint","IMPRINT",FACE,{"disambiguationData":[TD([[makeQuery(id+"F0.imprint","IMPRINT",EDGE,{"derivedFrom":sQuery(id+"F0.wireOp",EDGE,"E97.1.0.44")}),1.0]])]});
            var Q25;
            Q25=makeQuery(id+"F0.imprint","IMPRINT",FACE,{"disambiguationData":[TD([[makeQuery(id+"F0.imprint","IMPRINT",EDGE,{"derivedFrom":sQuery(id+"F0.wireOp",EDGE,"E45.MirrorCS")}),-1.0]])]});
            var Q26;
            {var subQ1=sQuery(id+"F0.wireOp",EDGE,"E13.MirrorCS");Q26=makeQuery(id+"F0.imprint","IMPRINT",FACE,{"disambiguationData":[TD([[makeQuery(id+"F0.imprint","IMPRINT",EDGE,{"derivedFrom":subQ1}),-1.0]])]});}
            var Q27;
            Q27=makeQuery(id+"F0.imprint","IMPRINT",FACE,{"disambiguationData":[TD([[makeQuery(id+"F0.imprint","IMPRINT",EDGE,{"derivedFrom":sQuery(id+"F0.wireOp",EDGE,"E12.MirrorCS")}),-1.0]])]});
            var Q28;
            Q28=makeQuery(id+"F0.imprint","IMPRINT",FACE,{"disambiguationData":[TD([[makeQuery(id+"F0.imprint","IMPRINT",EDGE,{"derivedFrom":sQuery(id+"F0.wireOp",EDGE,"E97.1.0.59")}),1.0]])]});
            var Q29;
            Q29=makeQuery(id+"F0.imprint","IMPRINT",FACE,{"disambiguationData":[TD([[makeQuery(id+"F0.imprint","IMPRINT",EDGE,{"derivedFrom":sQuery(id+"F0.wireOp",EDGE,"E97.1.0.108")}),1.0]])]});
            var Q30;
            {var subQ0=sQuery(id+"F0.wireOp",EDGE,"E17.MirrorCS");Q30=makeQuery(id+"F0.imprint","IMPRINT",FACE,{"disambiguationData":[TD([[makeQuery(id+"F0.imprint","IMPRINT",EDGE,{"derivedFrom":subQ0}),-1.0]])]});}
            var Q31;
            Q31=makeQuery(id+"F0.imprint","IMPRINT",FACE,{"disambiguationData":[TD([[makeQuery(id+"F0.imprint","IMPRINT",EDGE,{"derivedFrom":sQuery(id+"F0.wireOp",EDGE,"E97.1.0.94")}),1.0]])]});
            var Q32;
            Q32=makeQuery(id+"F0.imprint","IMPRINT",FACE,{"disambiguationData":[TD([[makeQuery(id+"F0.imprint","IMPRINT",EDGE,{"derivedFrom":sQuery(id+"F0.wireOp",EDGE,"E97.1.0.129")}),1.0]])]});
            var Q33;
            Q33=makeQuery(id+"F0.imprint","IMPRINT",FACE,{"disambiguationData":[TD([[makeQuery(id+"F0.imprint","IMPRINT",EDGE,{"derivedFrom":sQuery(id+"F0.wireOp",EDGE,"E24.MirrorCS")}),1.0]])]});
            var Q34;
            Q34=makeQuery(id+"F0.imprint","IMPRINT",FACE,{"disambiguationData":[TD([[makeQuery(id+"F0.imprint","IMPRINT",EDGE,{"derivedFrom":sQuery(id+"F0.wireOp",EDGE,"E97.1.0.112")}),1.0]])]});
            var Q35;
            Q35=makeQuery(id+"F0.imprint","IMPRINT",FACE,{"disambiguationData":[TD([[makeQuery(id+"F0.imprint","IMPRINT",EDGE,{"derivedFrom":sQuery(id+"F0.wireOp",EDGE,"E97.1.0.58")}),1.0]])]});
            var Q36;
            Q36=makeQuery(id+"F0.imprint","IMPRINT",FACE,{"disambiguationData":[TD([[makeQuery(id+"F0.imprint","IMPRINT",EDGE,{"derivedFrom":sQuery(id+"F0.wireOp",EDGE,"E19.MirrorCS")}),1.0]])]});
            var Q37;
            Q37=makeQuery(id+"F0.imprint","IMPRINT",FACE,{"disambiguationData":[TD([[makeQuery(id+"F0.imprint","IMPRINT",EDGE,{"derivedFrom":sQuery(id+"F0.wireOp",EDGE,"E22.MirrorCS")}),-1.0]])]});
            var Q38;
            Q38=makeQuery(id+"F0.imprint","IMPRINT",FACE,{"disambiguationData":[TD([[makeQuery(id+"F0.imprint","IMPRINT",EDGE,{"derivedFrom":sQuery(id+"F0.wireOp",EDGE,"E97.1.0.99")}),-1.0]])]});
            var Q39;
            Q39=makeQuery(id+"F0.imprint","IMPRINT",FACE,{"disambiguationData":[TD([[makeQuery(id+"F0.imprint","IMPRINT",EDGE,{"derivedFrom":sQuery(id+"F0.wireOp",EDGE,"E97.1.0.46")}),1.0]])]});
            var Q40;
            Q40=makeQuery(id+"F0.imprint","IMPRINT",FACE,{"disambiguationData":[TD([[makeQuery(id+"F0.imprint","IMPRINT",EDGE,{"derivedFrom":sQuery(id+"F0.wireOp",EDGE,"E97.1.0.48")}),-1.0]])]});
            var Q41;
            {var subQ1=sQuery(id+"F0.wireOp",EDGE,"E97.1.0.38");Q41=makeQuery(id+"F0.imprint","IMPRINT",FACE,{"disambiguationData":[TD([[makeQuery(id+"F0.imprint","IMPRINT",EDGE,{"derivedFrom":subQ1}),-1.0]])]});}
            var Q42;
            {var subQ1=sQuery(id+"F0.wireOp",EDGE,"E97.1.0.80");Q42=makeQuery(id+"F0.imprint","IMPRINT",FACE,{"disambiguationData":[TD([[makeQuery(id+"F0.imprint","IMPRINT",EDGE,{"derivedFrom":subQ1}),-1.0]])]});}
            var Q43;
            Q43=makeQuery(id+"F0.imprint","IMPRINT",FACE,{"disambiguationData":[TD([[makeQuery(id+"F0.imprint","IMPRINT",EDGE,{"derivedFrom":sQuery(id+"F0.wireOp",EDGE,"E97.1.0.55")}),1.0]])]});
            var Q44;
            {var subQ2=sQuery(id+"F0.wireOp",EDGE,"E97.1.0.49");Q44=makeQuery(id+"F0.imprint","IMPRINT",FACE,{"disambiguationData":[TD([[makeQuery(id+"F0.imprint","IMPRINT",EDGE,{"derivedFrom":subQ2}),-1.0]])]});}
            var Q45;
            Q45=makeQuery(id+"F0.imprint","IMPRINT",FACE,{"disambiguationData":[TD([[makeQuery(id+"F0.imprint","IMPRINT",EDGE,{"derivedFrom":sQuery(id+"F0.wireOp",EDGE,"E97.1.0.39")}),1.0]])]});
            var Q46;
            {var subQ1=sQuery(id+"F0.wireOp",EDGE,"E97.1.0.45");Q46=makeQuery(id+"F0.imprint","IMPRINT",FACE,{"disambiguationData":[TD([[makeQuery(id+"F0.imprint","IMPRINT",EDGE,{"derivedFrom":subQ1}),-1.0]])]});}
            var Q47;
            Q47=makeQuery(id+"F0.imprint","IMPRINT",FACE,{"disambiguationData":[TD([[makeQuery(id+"F0.imprint","IMPRINT",EDGE,{"derivedFrom":sQuery(id+"F0.wireOp",EDGE,"E97.1.0.65")}),-1.0]])]});
            var Q48;
            Q48=makeQuery(id+"F0.imprint","IMPRINT",FACE,{"disambiguationData":[TD([[makeQuery(id+"F0.imprint","IMPRINT",EDGE,{"derivedFrom":sQuery(id+"F0.wireOp",EDGE,"E97.1.0.47")}),1.0]])]});
            var Q49;
            Q49=makeQuery(id+"F0.imprint","IMPRINT",FACE,{"disambiguationData":[TD([[makeQuery(id+"F0.imprint","IMPRINT",EDGE,{"derivedFrom":sQuery(id+"F0.wireOp",EDGE,"E97.1.0.76")}),1.0]])]});
            var Q50;
            Q50=makeQuery(id+"F0.imprint","IMPRINT",FACE,{"disambiguationData":[TD([[makeQuery(id+"F0.imprint","IMPRINT",EDGE,{"derivedFrom":sQuery(id+"F0.wireOp",EDGE,"E97.1.0.70")}),1.0]])]});
            var Q51;
            Q51=makeQuery(id+"F0.imprint","IMPRINT",FACE,{"disambiguationData":[TD([[makeQuery(id+"F0.imprint","IMPRINT",EDGE,{"derivedFrom":sQuery(id+"F0.wireOp",EDGE,"E97.1.0.88")}),-1.0]])]});
            extrude(context, id + "F1", {"entities" : qUnion([Q0, Q1, Q2, Q3, Q4, Q5, Q6, Q7, Q8, Q9, Q10, Q11, Q12, Q13, Q14, Q15, Q16, Q17, Q18, Q19, Q20, Q21, Q22, Q23, Q24, Q25, Q26, Q27, Q28, Q29, Q30, Q31, Q32, Q33, Q34, Q35, Q36, Q37, Q38, Q39, Q40, Q41, Q42, Q43, Q44, Q45, Q46, Q47, Q48, Q49, Q50, Q51]), "oppositeDirection" : true, "depth" : 550 * mm, "offsetDistance" : 25 * mm});
        }
        {
            var Q0;
            {var subQ0=sQuery(id+"F0.wireOp",EDGE,"E88.bottom");Q0=makeQuery(id+"F0.imprint","IMPRINT",FACE,{"disambiguationData":[TD([[makeQuery(id+"F0.imprint","IMPRINT",EDGE,{"derivedFrom":subQ0}),-1.0]])]});}
            var Q1;
            {var subQ0=sQuery(id+"F0.wireOp",EDGE,"E97.1.0.4");Q1=makeQuery(id+"F0.imprint","IMPRINT",FACE,{"disambiguationData":[TD([[makeQuery(id+"F0.imprint","IMPRINT",EDGE,{"derivedFrom":subQ0}),-1.0]])]});}
            var Q2;
            Q2=makeQuery(id+"F0.imprint","IMPRINT",FACE,{"disambiguationData":[TD([[makeQuery(id+"F0.imprint","IMPRINT",EDGE,{"derivedFrom":sQuery(id+"F0.wireOp",EDGE,"E97.1.0.9")}),-1.0]])]});
            var Q3;
            Q3=makeQuery(id+"F0.imprint","IMPRINT",FACE,{"disambiguationData":[TD([[makeQuery(id+"F0.imprint","IMPRINT",EDGE,{"derivedFrom":sQuery(id+"F0.wireOp",EDGE,"E1.bottom")}),-1.0]])]});
            extrude(context, id + "F2", {"entities" : qUnion([Q0, Q1, Q2, Q3]), "oppositeDirection" : true, "depth" : 50 * mm, "offsetDistance" : 25 * mm});
        }
        {
            var Q0;
            {var subQ18=sQuery(id+"F0.wireOp",EDGE,"E97.2.0.50");Q0=makeQuery(id+"F0.imprint","IMPRINT",FACE,{"disambiguationData":[TD([[makeQuery(id+"F0.imprint","IMPRINT",EDGE,{"derivedFrom":subQ18}),1.0]])]});}
            var Q1;
            {var subQ2=sQuery(id+"F0.wireOp",EDGE,"E97.1.0.50");Q1=makeQuery(id+"F0.imprint","IMPRINT",FACE,{"disambiguationData":[TD([[makeQuery(id+"F0.imprint","IMPRINT",EDGE,{"derivedFrom":subQ2}),1.0]])]});}
            var Q2;
            {var subQ18=sQuery(id+"F0.wireOp",EDGE,"E0.bottom");Q2=makeQuery(id+"F0.imprint","IMPRINT",FACE,{"disambiguationData":[TD([[makeQuery(id+"F0.imprint","IMPRINT",EDGE,{"derivedFrom":subQ18}),1.0]])]});}
            extrude(context, id + "F3", {"entities" : qUnion([Q0, Q1, Q2]), "oppositeDirection" : true, "depth" : 50 * mm, "offsetDistance" : 25 * mm});
        }
        {
            var Q0;
            Q0=makeQuery(id+"F3.opExtrude","SWEPT_FACE",FACE,{"disambiguationData":[OSD([sQuery(id+"F0.wireOp",EDGE,"E97.1.0.51")])]});
            var sketch = newSketch(context, id + "F4", { "sketchPlane" : qUnion([Q0])});
            skLineSegment(sketch, "E99.bottom", {"start": v(-432.9, 2) * mm, "end": v(-478.9, 2) * mm});
            skLineSegment(sketch, "E99.top", {"start": v(-432.9, 48) * mm, "end": v(-478.9, 48) * mm});
            skLineSegment(sketch, "E99.left", {"start": v(-432.9, 2) * mm, "end": v(-432.9, 48) * mm});
            skLineSegment(sketch, "E99.right", {"start": v(-478.9, 2) * mm, "end": v(-478.9, 48) * mm});
            skPoint(sketch, "E99.middle", {"position": v(-455.9, 25) * mm});
            skLineSegment(sketch, "E100.bottom", {"start": v(-992.9, 2) * mm, "end": v(-1038.9, 2) * mm});
            skLineSegment(sketch, "E100.top", {"start": v(-992.9, 48) * mm, "end": v(-1038.9, 48) * mm});
            skLineSegment(sketch, "E100.left", {"start": v(-992.9, 2) * mm, "end": v(-992.9, 48) * mm});
            skLineSegment(sketch, "E100.right", {"start": v(-1038.9, 2) * mm, "end": v(-1038.9, 48) * mm});
            skPoint(sketch, "E100.middle", {"position": v(-1015.9, 25) * mm});
            skLineSegment(sketch, "E101.bottom", {"start": v(127.1, 2) * mm, "end": v(81.1, 2) * mm});
            skLineSegment(sketch, "E101.top", {"start": v(127.1, 48) * mm, "end": v(81.1, 48) * mm});
            skLineSegment(sketch, "E101.left", {"start": v(127.1, 2) * mm, "end": v(127.1, 48) * mm});
            skLineSegment(sketch, "E101.right", {"start": v(81.1, 2) * mm, "end": v(81.1, 48) * mm});
            skPoint(sketch, "E101.middle", {"position": v(104.1, 25) * mm});
            skSolve(sketch);
        }
        {
            var Q0;
            Q0=makeQuery(id+"F4.imprint","IMPRINT",FACE,{"disambiguationData":[TD([[makeQuery(id+"F4.imprint","IMPRINT",EDGE,{"derivedFrom":sQuery(id+"F4.wireOp",EDGE,"E100.bottom")}),-1.0]])]});
            extrude(context, id + "F5", {"entities" : qUnion([Q0]), "operationType" : NewBodyOperationType.REMOVE, "oppositeDirection" : true, "depth" : 1800 * mm, "offsetDistance" : 25 * mm});
        }
        {
            var Q0;
            Q0=makeQuery(id+"F4.imprint","IMPRINT",FACE,{"disambiguationData":[TD([[makeQuery(id+"F4.imprint","IMPRINT",EDGE,{"derivedFrom":sQuery(id+"F4.wireOp",EDGE,"E99.bottom")}),-1.0]])]});
            extrude(context, id + "F6", {"entities" : qUnion([Q0]), "operationType" : NewBodyOperationType.REMOVE, "oppositeDirection" : true, "depth" : 1800 * mm, "offsetDistance" : 25 * mm});
        }
        {
            var Q0;
            Q0=makeQuery(id+"F4.imprint","IMPRINT",FACE,{"disambiguationData":[TD([[makeQuery(id+"F4.imprint","IMPRINT",EDGE,{"derivedFrom":sQuery(id+"F4.wireOp",EDGE,"E101.bottom")}),-1.0]])]});
            extrude(context, id + "F7", {"entities" : qUnion([Q0]), "operationType" : NewBodyOperationType.REMOVE, "oppositeDirection" : true, "depth" : 1800 * mm, "offsetDistance" : 25 * mm});
        }
        {
            var Q0;
            Q0=makeQuery(id+"F3.opExtrude","CAP_FACE",FACE,{"disambiguationData":[OSD([sQuery(id+"F0.wireOp",EDGE,"E0.bottom"),sQuery(id+"F0.wireOp",EDGE,"E0.top"),sQuery(id+"F0.wireOp",EDGE,"E0.left"),sQuery(id+"F0.wireOp",EDGE,"E0.right")])],"isStart":false});
            var sketch = newSketch(context, id + "F8", { "sketchPlane" : qUnion([Q0])});
            skLineSegment(sketch, "E102.bottom", {"start": v(1040.9, 169.44) * mm, "end": v(990.9, 169.44) * mm});
            skLineSegment(sketch, "E102.top", {"start": v(1040.9, 219.44) * mm, "end": v(990.9, 219.44) * mm});
            skLineSegment(sketch, "E102.left", {"start": v(1040.9, 169.44) * mm, "end": v(1040.9, 219.44) * mm});
            skLineSegment(sketch, "E102.right", {"start": v(990.9, 169.44) * mm, "end": v(990.9, 219.44) * mm});
            skPoint(sketch, "E102.middle", {"position": v(1015.9, 194.44) * mm});
            skLineSegment(sketch, "E103.bottom", {"start": v(-129.1, 169.44) * mm, "end": v(-79.1, 169.44) * mm});
            skLineSegment(sketch, "E103.top", {"start": v(-129.1, 219.44) * mm, "end": v(-79.1, 219.44) * mm});
            skLineSegment(sketch, "E103.left", {"start": v(-129.1, 169.44) * mm, "end": v(-129.1, 219.44) * mm});
            skLineSegment(sketch, "E103.right", {"start": v(-79.1, 169.44) * mm, "end": v(-79.1, 219.44) * mm});
            skPoint(sketch, "E103.middle", {"position": v(-104.1, 194.44) * mm});
            skLineSegment(sketch, "E104.bottom", {"start": v(1040.9, 1869.44) * mm, "end": v(990.9, 1869.44) * mm});
            skLineSegment(sketch, "E104.top", {"start": v(1040.9, 1819.44) * mm, "end": v(990.9, 1819.44) * mm});
            skLineSegment(sketch, "E104.left", {"start": v(1040.9, 1869.44) * mm, "end": v(1040.9, 1819.44) * mm});
            skLineSegment(sketch, "E104.right", {"start": v(990.9, 1869.44) * mm, "end": v(990.9, 1819.44) * mm});
            skLineSegment(sketch, "E105.bottom", {"start": v(-129.1, 1869.44) * mm, "end": v(-79.1, 1869.44) * mm});
            skLineSegment(sketch, "E105.top", {"start": v(-129.1, 1819.44) * mm, "end": v(-79.1, 1819.44) * mm});
            skLineSegment(sketch, "E105.left", {"start": v(-129.1, 1869.44) * mm, "end": v(-129.1, 1819.44) * mm});
            skLineSegment(sketch, "E105.right", {"start": v(-79.1, 1869.44) * mm, "end": v(-79.1, 1819.44) * mm});
            skSolve(sketch);
        }
        {
            var Q0;
            Q0=makeQuery(id+"F8.imprint","IMPRINT",FACE,{"disambiguationData":[TD([[makeQuery(id+"F8.imprint","IMPRINT",EDGE,{"derivedFrom":sQuery(id+"F8.wireOp",EDGE,"E102.bottom")}),-1.0]])]});
            var Q1;
            Q1=makeQuery(id+"F8.imprint","IMPRINT",FACE,{"disambiguationData":[TD([[makeQuery(id+"F8.imprint","IMPRINT",EDGE,{"derivedFrom":sQuery(id+"F8.wireOp",EDGE,"E103.bottom")}),1.0]])]});
            var Q2;
            Q2=makeQuery(id+"F8.imprint","IMPRINT",FACE,{"disambiguationData":[TD([[makeQuery(id+"F8.imprint","IMPRINT",EDGE,{"derivedFrom":sQuery(id+"F8.wireOp",EDGE,"E105.bottom")}),-1.0]])]});
            var Q3;
            Q3=makeQuery(id+"F8.imprint","IMPRINT",FACE,{"disambiguationData":[TD([[makeQuery(id+"F8.imprint","IMPRINT",EDGE,{"derivedFrom":sQuery(id+"F8.wireOp",EDGE,"E104.bottom")}),1.0]])]});
            extrude(context, id + "F9", {"entities" : qUnion([Q0, Q1, Q2, Q3]), "depth" : 450 * mm, "offsetDistance" : 25 * mm});
        }
        {
            var Q0;
            {var subQ18=sQuery(id+"F0.wireOp",EDGE,"E0.bottom");Q0=makeQuery(id+"F0.imprint","IMPRINT",FACE,{"disambiguationData":[TD([[makeQuery(id+"F0.imprint","IMPRINT",EDGE,{"derivedFrom":subQ18}),1.0]])]});}
            var sketch = newSketch(context, id + "F10", { "sketchPlane" : qUnion([Q0])});
            skLineSegment(sketch, "E106", {"start": v(279.27, 194.44) * mm, "end": v(-1301.33, 194.44) * mm, "construction": true});
            skLineSegment(sketch, "E107", {"start": v(-990.9, 169.44) * mm, "end": v(-990.9, 194.44) * mm, "construction": true});
            skPoint(sketch, "E108", {"position": v(-990.9, 181.94) * mm});
            skLineSegment(sketch, "E109", {"start": v(-1155.92, 181.94) * mm, "end": v(236.2, 181.94) * mm, "construction": true});
            skCircle(sketch, "E110", {"center": v(-1015.9, 194.44) * mm, "radius": 3 * mm});
            skCircle(sketch, "E111.0.1.0", {"center": v(-1015.9, 524.44) * mm, "radius": 3 * mm});
            skCircle(sketch, "E111.0.2.0", {"center": v(-1015.9, 854.44) * mm, "radius": 3 * mm});
            skCircle(sketch, "E111.0.3.0", {"center": v(-1015.9, 1184.44) * mm, "radius": 3 * mm});
            skCircle(sketch, "E111.0.4.0", {"center": v(-1015.9, 1514.44) * mm, "radius": 3 * mm});
            skCircle(sketch, "E111.0.5.0", {"center": v(-1015.9, 1844.44) * mm, "radius": 3 * mm});
            skLineSegment(sketch, "E111.direction1", {"start": v(-1015.9, 194.44) * mm, "end": v(-990.9, 194.44) * mm, "construction": true});
            skLineSegment(sketch, "E111.direction2", {"start": v(-1015.9, 194.44) * mm, "end": v(-1015.9, 524.44) * mm, "construction": true});
            skCircle(sketch, "E112", {"center": v(103.63, 194.44) * mm, "radius": 3 * mm});
            skCircle(sketch, "E113.0.1.0", {"center": v(103.63, 524.44) * mm, "radius": 3 * mm});
            skCircle(sketch, "E113.0.2.0", {"center": v(103.63, 854.44) * mm, "radius": 3 * mm});
            skCircle(sketch, "E113.0.3.0", {"center": v(103.63, 1184.44) * mm, "radius": 3 * mm});
            skCircle(sketch, "E113.0.4.0", {"center": v(103.63, 1514.44) * mm, "radius": 3 * mm});
            skCircle(sketch, "E113.0.5.0", {"center": v(103.63, 1844.44) * mm, "radius": 3 * mm});
            skLineSegment(sketch, "E113.direction1", {"start": v(103.63, 194.44) * mm, "end": v(128.63, 194.44) * mm, "construction": true});
            skLineSegment(sketch, "E113.direction2", {"start": v(103.63, 194.44) * mm, "end": v(103.63, 524.44) * mm, "construction": true});
            skCircle(sketch, "E114", {"center": v(-443.4, 194.44) * mm, "radius": 3 * mm});
            skCircle(sketch, "E115.0.1.0", {"center": v(-443.4, 524.44) * mm, "radius": 3 * mm});
            skCircle(sketch, "E115.0.2.0", {"center": v(-443.4, 854.44) * mm, "radius": 3 * mm});
            skCircle(sketch, "E115.0.3.0", {"center": v(-443.4, 1184.44) * mm, "radius": 3 * mm});
            skCircle(sketch, "E115.0.4.0", {"center": v(-443.4, 1514.44) * mm, "radius": 3 * mm});
            skCircle(sketch, "E115.0.5.0", {"center": v(-443.4, 1844.44) * mm, "radius": 3 * mm});
            skLineSegment(sketch, "E115.direction1", {"start": v(-443.4, 194.44) * mm, "end": v(-404.15, 194.44) * mm, "construction": true});
            skLineSegment(sketch, "E115.direction2", {"start": v(-443.4, 194.44) * mm, "end": v(-443.4, 524.44) * mm, "construction": true});
            skCircle(sketch, "E116", {"center": v(-468.4, 194.44) * mm, "radius": 3 * mm});
            skCircle(sketch, "E117.0.1.0", {"center": v(-468.4, 524.44) * mm, "radius": 3 * mm});
            skCircle(sketch, "E117.0.2.0", {"center": v(-468.4, 854.44) * mm, "radius": 3 * mm});
            skCircle(sketch, "E117.0.3.0", {"center": v(-468.4, 1184.44) * mm, "radius": 3 * mm});
            skCircle(sketch, "E117.0.4.0", {"center": v(-468.4, 1514.44) * mm, "radius": 3 * mm});
            skCircle(sketch, "E117.0.5.0", {"center": v(-468.4, 1844.44) * mm, "radius": 3 * mm});
            skLineSegment(sketch, "E117.direction1", {"start": v(-517.4, 194.44) * mm, "end": v(-468.4, 194.44) * mm, "construction": true});
            skLineSegment(sketch, "E117.direction2", {"start": v(-468.4, 194.44) * mm, "end": v(-468.4, 524.44) * mm, "construction": true});
            skCircle(sketch, "E118", {"center": v(-906.47, 181.94) * mm, "radius": 7.3 * mm});
            skSolve(sketch);
        }
        {
            var Q0;
            Q0=makeQuery(id+"F10.imprint","IMPRINT",FACE,{"disambiguationData":[TD([[makeQuery(id+"F10.imprint","IMPRINT",EDGE,{"derivedFrom":sQuery(id+"F10.wireOp",EDGE,"E110")}),1.0]])]});
            var Q1;
            Q1=makeQuery(id+"F10.imprint","IMPRINT",FACE,{"disambiguationData":[TD([[makeQuery(id+"F10.imprint","IMPRINT",EDGE,{"derivedFrom":sQuery(id+"F10.wireOp",EDGE,"E111.0.1.0")}),1.0]])]});
            var Q2;
            Q2=makeQuery(id+"F10.imprint","IMPRINT",FACE,{"disambiguationData":[TD([[makeQuery(id+"F10.imprint","IMPRINT",EDGE,{"derivedFrom":sQuery(id+"F10.wireOp",EDGE,"E111.0.2.0")}),1.0]])]});
            var Q3;
            Q3=makeQuery(id+"F10.imprint","IMPRINT",FACE,{"disambiguationData":[TD([[makeQuery(id+"F10.imprint","IMPRINT",EDGE,{"derivedFrom":sQuery(id+"F10.wireOp",EDGE,"E111.0.3.0")}),1.0]])]});
            var Q4;
            Q4=makeQuery(id+"F10.imprint","IMPRINT",FACE,{"disambiguationData":[TD([[makeQuery(id+"F10.imprint","IMPRINT",EDGE,{"derivedFrom":sQuery(id+"F10.wireOp",EDGE,"E111.0.4.0")}),1.0]])]});
            var Q5;
            Q5=makeQuery(id+"F10.imprint","IMPRINT",FACE,{"disambiguationData":[TD([[makeQuery(id+"F10.imprint","IMPRINT",EDGE,{"derivedFrom":sQuery(id+"F10.wireOp",EDGE,"E111.0.5.0")}),1.0]])]});
            var Q6;
            Q6=sQuery(id+"F10.wireOp",EDGE,"E110");
            var Q7;
            Q7=sQuery(id+"F10.wireOp",EDGE,"E111.0.1.0");
            extrude(context, id + "F11", {"entities" : qUnion([Q0, Q1, Q2, Q3, Q4, Q5]), "operationType" : NewBodyOperationType.REMOVE, "surfaceEntities" : qUnion([Q6, Q7]), "oppositeDirection" : true, "depth" : 25 * mm, "offsetDistance" : 25 * mm});
        }
        {
            var Q0;
            Q0=makeQuery(id+"F10.imprint","IMPRINT",FACE,{"disambiguationData":[TD([[makeQuery(id+"F10.imprint","IMPRINT",EDGE,{"derivedFrom":sQuery(id+"F10.wireOp",EDGE,"E113.0.4.0")}),1.0]])]});
            var Q1;
            Q1=makeQuery(id+"F10.imprint","IMPRINT",FACE,{"disambiguationData":[TD([[makeQuery(id+"F10.imprint","IMPRINT",EDGE,{"derivedFrom":sQuery(id+"F10.wireOp",EDGE,"E113.0.2.0")}),1.0]])]});
            var Q2;
            Q2=makeQuery(id+"F10.imprint","IMPRINT",FACE,{"disambiguationData":[TD([[makeQuery(id+"F10.imprint","IMPRINT",EDGE,{"derivedFrom":sQuery(id+"F10.wireOp",EDGE,"E113.0.1.0")}),1.0]])]});
            var Q3;
            Q3=makeQuery(id+"F10.imprint","IMPRINT",FACE,{"disambiguationData":[TD([[makeQuery(id+"F10.imprint","IMPRINT",EDGE,{"derivedFrom":sQuery(id+"F10.wireOp",EDGE,"E112")}),1.0]])]});
            var Q4;
            Q4=makeQuery(id+"F10.imprint","IMPRINT",FACE,{"disambiguationData":[TD([[makeQuery(id+"F10.imprint","IMPRINT",EDGE,{"derivedFrom":sQuery(id+"F10.wireOp",EDGE,"E113.0.3.0")}),1.0]])]});
            var Q5;
            Q5=makeQuery(id+"F10.imprint","IMPRINT",FACE,{"disambiguationData":[TD([[makeQuery(id+"F10.imprint","IMPRINT",EDGE,{"derivedFrom":sQuery(id+"F10.wireOp",EDGE,"E113.0.5.0")}),1.0]])]});
            extrude(context, id + "F12", {"entities" : qUnion([Q0, Q1, Q2, Q3, Q4, Q5]), "operationType" : NewBodyOperationType.REMOVE, "oppositeDirection" : true, "depth" : 25 * mm, "offsetDistance" : 25 * mm});
        }
        {
            var Q0;
            Q0=makeQuery(id+"F10.imprint","IMPRINT",FACE,{"disambiguationData":[TD([[makeQuery(id+"F10.imprint","IMPRINT",EDGE,{"derivedFrom":sQuery(id+"F10.wireOp",EDGE,"E116")}),1.0]])]});
            var Q1;
            Q1=makeQuery(id+"F10.imprint","IMPRINT",FACE,{"disambiguationData":[TD([[makeQuery(id+"F10.imprint","IMPRINT",EDGE,{"derivedFrom":sQuery(id+"F10.wireOp",EDGE,"E117.0.1.0")}),1.0]])]});
            var Q2;
            Q2=makeQuery(id+"F10.imprint","IMPRINT",FACE,{"disambiguationData":[TD([[makeQuery(id+"F10.imprint","IMPRINT",EDGE,{"derivedFrom":sQuery(id+"F10.wireOp",EDGE,"E117.0.2.0")}),1.0]])]});
            var Q3;
            Q3=makeQuery(id+"F10.imprint","IMPRINT",FACE,{"disambiguationData":[TD([[makeQuery(id+"F10.imprint","IMPRINT",EDGE,{"derivedFrom":sQuery(id+"F10.wireOp",EDGE,"E117.0.5.0")}),1.0]])]});
            var Q4;
            Q4=makeQuery(id+"F10.imprint","IMPRINT",FACE,{"disambiguationData":[TD([[makeQuery(id+"F10.imprint","IMPRINT",EDGE,{"derivedFrom":sQuery(id+"F10.wireOp",EDGE,"E117.0.3.0")}),1.0]])]});
            var Q5;
            Q5=makeQuery(id+"F10.imprint","IMPRINT",FACE,{"disambiguationData":[TD([[makeQuery(id+"F10.imprint","IMPRINT",EDGE,{"derivedFrom":sQuery(id+"F10.wireOp",EDGE,"E117.0.4.0")}),1.0]])]});
            var Q6;
            Q6=sQuery(id+"F10.wireOp",EDGE,"KcUSZxaL-kojM-k7IY-Rv9K-FD4xScU8XWQF");
            extrude(context, id + "F13", {"entities" : qUnion([Q0, Q1, Q2, Q3, Q4, Q5]), "operationType" : NewBodyOperationType.REMOVE, "surfaceEntities" : qUnion([Q6]), "oppositeDirection" : true, "depth" : 25 * mm, "offsetDistance" : 25 * mm});
        }
        {
            var Q0;
            Q0=makeQuery(id+"F10.imprint","IMPRINT",FACE,{"disambiguationData":[TD([[makeQuery(id+"F10.imprint","IMPRINT",EDGE,{"derivedFrom":sQuery(id+"F10.wireOp",EDGE,"E114")}),1.0]])]});
            var Q1;
            Q1=makeQuery(id+"F10.imprint","IMPRINT",FACE,{"disambiguationData":[TD([[makeQuery(id+"F10.imprint","IMPRINT",EDGE,{"derivedFrom":sQuery(id+"F10.wireOp",EDGE,"E115.0.1.0")}),1.0]])]});
            var Q2;
            Q2=makeQuery(id+"F10.imprint","IMPRINT",FACE,{"disambiguationData":[TD([[makeQuery(id+"F10.imprint","IMPRINT",EDGE,{"derivedFrom":sQuery(id+"F10.wireOp",EDGE,"E115.0.2.0")}),1.0]])]});
            var Q3;
            Q3=makeQuery(id+"F10.imprint","IMPRINT",FACE,{"disambiguationData":[TD([[makeQuery(id+"F10.imprint","IMPRINT",EDGE,{"derivedFrom":sQuery(id+"F10.wireOp",EDGE,"E115.0.3.0")}),1.0]])]});
            var Q4;
            Q4=makeQuery(id+"F10.imprint","IMPRINT",FACE,{"disambiguationData":[TD([[makeQuery(id+"F10.imprint","IMPRINT",EDGE,{"derivedFrom":sQuery(id+"F10.wireOp",EDGE,"E115.0.4.0")}),1.0]])]});
            var Q5;
            Q5=makeQuery(id+"F10.imprint","IMPRINT",FACE,{"disambiguationData":[TD([[makeQuery(id+"F10.imprint","IMPRINT",EDGE,{"derivedFrom":sQuery(id+"F10.wireOp",EDGE,"E115.0.5.0")}),1.0]])]});
            extrude(context, id + "F14", {"entities" : qUnion([Q0, Q1, Q2, Q3, Q4, Q5]), "operationType" : NewBodyOperationType.REMOVE, "oppositeDirection" : true, "depth" : 25 * mm, "offsetDistance" : 25 * mm});
        }
        {
            var Q0;
            Q0=makeQuery(id+"F0.imprint","IMPRINT",FACE,{"disambiguationData":[TD([[makeQuery(id+"F0.imprint","IMPRINT",EDGE,{"derivedFrom":sQuery(id+"F0.wireOp",EDGE,"E1.bottom")}),-1.0]])]});
            var sketch = newSketch(context, id + "F15", { "sketchPlane" : qUnion([Q0])});
            skLineSegment(sketch, "E119", {"start": v(-480.9, 194.44) * mm, "end": v(-990.9, 194.44) * mm, "construction": true});
            skCircle(sketch, "E120", {"center": v(-890.9, 194.44) * mm, "radius": 3 * mm});
            skCircle(sketch, "E121", {"center": v(-580.9, 194.44) * mm, "radius": 3 * mm});
            skCircle(sketch, "E122", {"center": v(-735.9, 194.44) * mm, "radius": 3 * mm});
            skLineSegment(sketch, "E123", {"start": v(-975.5, 181.94) * mm, "end": v(-498.06, 181.94) * mm, "construction": true});
            skCircle(sketch, "E124", {"center": v(-630.9, 181.94) * mm, "radius": 3 * mm});
            skCircle(sketch, "E125", {"center": v(-840.9, 181.94) * mm, "radius": 3 * mm});
            skSolve(sketch);
        }
        {
            var Q0;
            Q0 = qSketchRegion(id + "F15", true);
            extrude(context, id + "F16", {"entities" : qUnion([Q0]), "operationType" : NewBodyOperationType.REMOVE, "oppositeDirection" : true, "depth" : 55 * mm, "offsetDistance" : 25 * mm});
        }
        {
            var Q0;
            Q0=makeQuery(id+"F0.imprint","IMPRINT",FACE,{"disambiguationData":[TD([[makeQuery(id+"F0.imprint","IMPRINT",EDGE,{"derivedFrom":sQuery(id+"F0.wireOp",EDGE,"E97.1.0.9")}),-1.0]])]});
            var sketch = newSketch(context, id + "F17", { "sketchPlane" : qUnion([Q0])});
            skLineSegment(sketch, "E126", {"start": v(-430.9, 194.44) * mm, "end": v(86.3, 194.44) * mm, "construction": true});
            skCircle(sketch, "E127", {"center": v(-330.9, 194.44) * mm, "radius": 3 * mm});
            skCircle(sketch, "E128", {"center": v(-175.9, 194.44) * mm, "radius": 3 * mm});
            skCircle(sketch, "E129", {"center": v(-20.9, 194.44) * mm, "radius": 3.2 * mm});
            skLineSegment(sketch, "E130", {"start": v(-421.6, 181.94) * mm, "end": v(70.65, 181.94) * mm, "construction": true});
            skCircle(sketch, "E131", {"center": v(-280.9, 181.94) * mm, "radius": 3 * mm});
            skCircle(sketch, "E132", {"center": v(-70.9, 181.94) * mm, "radius": 3 * mm});
            skSolve(sketch);
        }
        {
            var Q0;
            Q0 = qSketchRegion(id + "F17", true);
            extrude(context, id + "F18", {"entities" : qUnion([Q0]), "operationType" : NewBodyOperationType.REMOVE, "oppositeDirection" : true, "depth" : 55 * mm, "offsetDistance" : 25 * mm});
        }
        {
            var Q0;
            {var subQ0=sQuery(id+"F0.wireOp",EDGE,"E97.1.0.4");Q0=makeQuery(id+"F0.imprint","IMPRINT",FACE,{"disambiguationData":[TD([[makeQuery(id+"F0.imprint","IMPRINT",EDGE,{"derivedFrom":subQ0}),-1.0]])]});}
            var sketch = newSketch(context, id + "F19", { "sketchPlane" : qUnion([Q0])});
            skLineSegment(sketch, "E133", {"start": v(-430.9, 1844.44) * mm, "end": v(87.3, 1844.44) * mm, "construction": true});
            skCircle(sketch, "E134", {"center": v(-330.9, 1844.44) * mm, "radius": 3 * mm});
            skCircle(sketch, "E135", {"center": v(-175.9, 1844.44) * mm, "radius": 3 * mm});
            skCircle(sketch, "E136", {"center": v(-20.9, 1844.44) * mm, "radius": 3 * mm});
            skSolve(sketch);
        }
        {
            var Q0;
            Q0 = qSketchRegion(id + "F19", true);
            extrude(context, id + "F20", {"entities" : qUnion([Q0]), "operationType" : NewBodyOperationType.REMOVE, "oppositeDirection" : true, "depth" : 55 * mm, "offsetDistance" : 25 * mm});
        }
        {
            var Q0;
            {var subQ0=sQuery(id+"F0.wireOp",EDGE,"E88.bottom");Q0=makeQuery(id+"F0.imprint","IMPRINT",FACE,{"disambiguationData":[TD([[makeQuery(id+"F0.imprint","IMPRINT",EDGE,{"derivedFrom":subQ0}),-1.0]])]});}
            var sketch = newSketch(context, id + "F21", { "sketchPlane" : qUnion([Q0])});
            skLineSegment(sketch, "E137", {"start": v(-990.9, 1844.44) * mm, "end": v(-475.19, 1844.44) * mm, "construction": true});
            skCircle(sketch, "E138", {"center": v(-890.9, 1844.44) * mm, "radius": 3 * mm});
            skCircle(sketch, "E139", {"center": v(-735.9, 1844.44) * mm, "radius": 3 * mm});
            skCircle(sketch, "E140", {"center": v(-580.9, 1844.44) * mm, "radius": 3 * mm});
            skSolve(sketch);
        }
        {
            var Q0;
            Q0 = qSketchRegion(id + "F21", true);
            extrude(context, id + "F22", {"entities" : qUnion([Q0]), "operationType" : NewBodyOperationType.REMOVE, "oppositeDirection" : true, "depth" : 55 * mm, "offsetDistance" : 25 * mm});
        }
        {
            var Q0;
            Q0=makeQuery(id+"F3.opExtrude","SWEPT_FACE",FACE,{"disambiguationData":[OSD([sQuery(id+"F0.wireOp",EDGE,"E98")])]});
            var sketch = newSketch(context, id + "F23", { "sketchPlane" : qUnion([Q0])});
            skCircle(sketch, "E141", {"center": v(26.2, 194.44) * mm, "radius": 3 * mm});
            skCircle(sketch, "E142.0.1.0", {"center": v(26.2, 524.44) * mm, "radius": 3 * mm});
            skCircle(sketch, "E142.0.2.0", {"center": v(26.2, 854.44) * mm, "radius": 3 * mm});
            skCircle(sketch, "E142.0.3.0", {"center": v(26.2, 1184.44) * mm, "radius": 3 * mm});
            skCircle(sketch, "E142.0.4.0", {"center": v(26.2, 1514.44) * mm, "radius": 3 * mm});
            skCircle(sketch, "E142.0.5.0", {"center": v(26.2, 1844.44) * mm, "radius": 3 * mm});
            skLineSegment(sketch, "E142.direction1", {"start": v(26.2, 194.44) * mm, "end": v(51.22, 194.44) * mm, "construction": true});
            skLineSegment(sketch, "E142.direction2", {"start": v(26.2, 194.44) * mm, "end": v(26.2, 524.44) * mm, "construction": true});
            skSolve(sketch);
        }
        {
            var Q0;
            Q0 = qSketchRegion(id + "F23", true);
            extrude(context, id + "F24", {"entities" : qUnion([Q0]), "operationType" : NewBodyOperationType.REMOVE, "oppositeDirection" : true, "depth" : 25 * mm, "offsetDistance" : 25 * mm});
        }
        {
            var Q0;
            Q0=makeQuery(id+"F9.opExtrude","SWEPT_FACE",FACE,{"disambiguationData":[OSD([sQuery(id+"F8.wireOp",EDGE,"E103.left")])]});
            var sketch = newSketch(context, id + "F25", { "sketchPlane" : qUnion([Q0])});
            skCircle(sketch, "E143", {"center": v(100, 194.44) * mm, "radius": 3 * mm});
            skCircle(sketch, "E144", {"center": v(275, 194.44) * mm, "radius": 3 * mm});
            skCircle(sketch, "E145", {"center": v(450, 194.44) * mm, "radius": 3 * mm});
            skLineSegment(sketch, "E146", {"start": v(100, 194.44) * mm, "end": v(450, 194.44) * mm, "construction": true});
            skSolve(sketch);
        }
        {
            var Q0;
            Q0 = qSketchRegion(id + "F25", true);
            extrude(context, id + "F26", {"entities" : qUnion([Q0]), "operationType" : NewBodyOperationType.REMOVE, "oppositeDirection" : true, "depth" : 55 * mm, "offsetDistance" : 25 * mm});
        }
        {
            var Q0;
            Q0=makeQuery(id+"F9.opExtrude","SWEPT_FACE",FACE,{"disambiguationData":[OSD([sQuery(id+"F8.wireOp",EDGE,"E105.left")])]});
            var sketch = newSketch(context, id + "F27", { "sketchPlane" : qUnion([Q0])});
            skCircle(sketch, "E147", {"center": v(100, 1844.44) * mm, "radius": 3 * mm});
            skCircle(sketch, "E148", {"center": v(275, 1844.44) * mm, "radius": 3 * mm});
            skCircle(sketch, "E149", {"center": v(450, 1844.44) * mm, "radius": 3 * mm});
            skLineSegment(sketch, "E150", {"start": v(100, 1844.44) * mm, "end": v(450, 1844.44) * mm, "construction": true});
            skSolve(sketch);
        }
        {
            var Q0;
            Q0 = qSketchRegion(id + "F27", true);
            extrude(context, id + "F28", {"entities" : qUnion([Q0]), "operationType" : NewBodyOperationType.REMOVE, "oppositeDirection" : true, "depth" : 55 * mm, "offsetDistance" : 25 * mm});
        }
        {
            var Q0;
            Q0=makeQuery(id+"F9.opExtrude","CAP_FACE",FACE,{"disambiguationData":[OSD([sQuery(id+"F8.wireOp",EDGE,"E103.bottom"),sQuery(id+"F8.wireOp",EDGE,"E103.top"),sQuery(id+"F8.wireOp",EDGE,"E103.left"),sQuery(id+"F8.wireOp",EDGE,"E103.right")])],"isStart":false});
            var sketch = newSketch(context, id + "F29", { "sketchPlane" : qUnion([Q0])});
            skLineSegment(sketch, "E151.bottom", {"start": v(-129.1, 1869.44) * mm, "end": v(-79.1, 1869.44) * mm});
            skLineSegment(sketch, "E151.top", {"start": v(-129.1, 69.44) * mm, "end": v(-79.1, 69.44) * mm});
            skLineSegment(sketch, "E151.left", {"start": v(-129.1, 1869.44) * mm, "end": v(-129.1, 69.44) * mm});
            skLineSegment(sketch, "E151.right", {"start": v(-79.1, 1869.44) * mm, "end": v(-79.1, 69.44) * mm});
            skSolve(sketch);
        }
        {
            var Q0;
            Q0 = qSketchRegion(id + "F29", true);
            extrude(context, id + "F30", {"entities" : qUnion([Q0]), "depth" : 50 * mm, "offsetDistance" : 25 * mm});
        }
        {
            var Q0;
            Q0=makeQuery(id+"F30.opExtrude","SWEPT_FACE",FACE,{"disambiguationData":[OSD([sQuery(id+"F29.wireOp",EDGE,"E151.left")])]});
            var sketch = newSketch(context, id + "F31", { "sketchPlane" : qUnion([Q0])});
            skCircle(sketch, "E152", {"center": v(524.02, 194.44) * mm, "radius": 3 * mm});
            skCircle(sketch, "E153.0.1.0", {"center": v(524.02, 524.44) * mm, "radius": 3 * mm});
            skCircle(sketch, "E153.0.2.0", {"center": v(524.02, 854.44) * mm, "radius": 3 * mm});
            skCircle(sketch, "E153.0.3.0", {"center": v(524.02, 1184.44) * mm, "radius": 3 * mm});
            skCircle(sketch, "E153.0.4.0", {"center": v(524.02, 1514.44) * mm, "radius": 3 * mm});
            skCircle(sketch, "E153.0.5.0", {"center": v(524.02, 1844.44) * mm, "radius": 3 * mm});
            skLineSegment(sketch, "E153.direction1", {"start": v(524.02, 194.44) * mm, "end": v(549.02, 194.44) * mm, "construction": true});
            skLineSegment(sketch, "E153.direction2", {"start": v(524.02, 194.44) * mm, "end": v(524.02, 524.44) * mm, "construction": true});
            skSolve(sketch);
        }
        {
            var Q0;
            Q0 = qSketchRegion(id + "F31", true);
            extrude(context, id + "F32", {"entities" : qUnion([Q0]), "operationType" : NewBodyOperationType.REMOVE, "oppositeDirection" : true, "depth" : 25 * mm, "offsetDistance" : 25 * mm});
        }
        {
            var Q0;
            Q0=makeQuery(id+"F30.opExtrude","SWEPT_FACE",FACE,{"disambiguationData":[OSD([sQuery(id+"F29.wireOp",EDGE,"E151.bottom")])]});
            var sketch = newSketch(context, id + "F33", { "sketchPlane" : qUnion([Q0])});
            skLineSegment(sketch, "E154.bottom", {"start": v(81.1, 502) * mm, "end": v(127.1, 502) * mm});
            skLineSegment(sketch, "E154.top", {"start": v(81.1, 548) * mm, "end": v(127.1, 548) * mm});
            skLineSegment(sketch, "E154.left", {"start": v(81.1, 502) * mm, "end": v(81.1, 548) * mm});
            skLineSegment(sketch, "E154.right", {"start": v(127.1, 502) * mm, "end": v(127.1, 548) * mm});
            skSolve(sketch);
        }
        {
            var Q0;
            Q0=makeQuery(id+"F33.imprint","IMPRINT",FACE,{"disambiguationData":[TD([[makeQuery(id+"F33.imprint","IMPRINT",EDGE,{"derivedFrom":sQuery(id+"F33.wireOp",EDGE,"E154.bottom")}),1.0]])]});
            extrude(context, id + "F34", {"entities" : qUnion([Q0]), "operationType" : NewBodyOperationType.REMOVE, "oppositeDirection" : true, "depth" : 1800 * mm, "offsetDistance" : 25 * mm});
        }
    });
